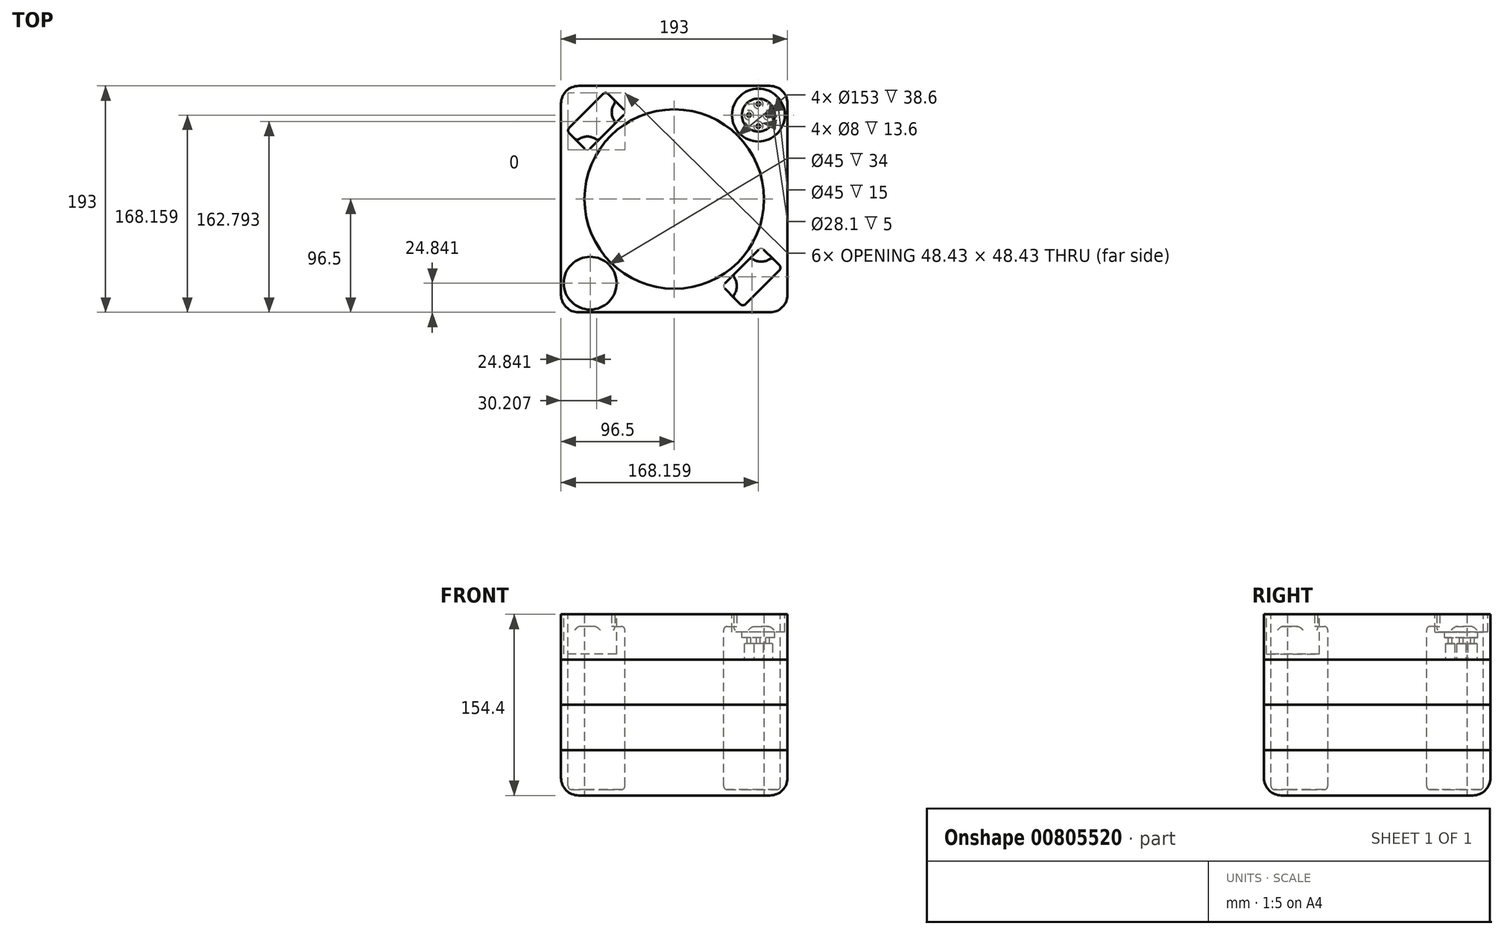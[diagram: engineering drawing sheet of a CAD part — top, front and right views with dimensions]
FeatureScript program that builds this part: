
annotation { "Feature Type Name" : "Feature", "Feature Type Description" : "" }
export const myFeature = defineFeature(function(context is Context, id is Id, definition is map)
    precondition{}
    {
        {
            var Q0;
            Q0=qCreatedBy(makeId("Top.planeOp"),FACE);
            cPlane(context, id + "F0", {"entities" : qUnion([Q0]), "cplaneType" : CPlaneType.OFFSET, "offset" : 0 * mm, "width" : 150 * mm, "height" : 150 * mm});
        }
        {
            var Q0;
            Q0=qCreatedBy(makeId("Top.planeOp"),FACE);
            cPlane(context, id + "F1", {"entities" : qUnion([Q0]), "cplaneType" : CPlaneType.OFFSET, "offset" : 38.6 * mm, "width" : 150 * mm, "height" : 150 * mm});
        }
        {
            var Q0;
            Q0=qCreatedBy(makeId("Top.planeOp"),FACE);
            cPlane(context, id + "F2", {"entities" : qUnion([Q0]), "cplaneType" : CPlaneType.OFFSET, "offset" : 77.2 * mm, "width" : 150 * mm, "height" : 150 * mm});
        }
        {
            var Q0;
            Q0=qCreatedBy(makeId("Top.planeOp"),FACE);
            cPlane(context, id + "F3", {"entities" : qUnion([Q0]), "cplaneType" : CPlaneType.OFFSET, "offset" : 115.8 * mm, "width" : 150 * mm, "height" : 150 * mm});
        }
        {
            var Q0;
            Q0=qCreatedBy(makeId("Top.planeOp"),FACE);
            cPlane(context, id + "F4", {"entities" : qUnion([Q0]), "cplaneType" : CPlaneType.OFFSET, "offset" : 154.4 * mm, "width" : 150 * mm, "height" : 150 * mm});
        }
        {
            var Q0;
            Q0=qCreatedBy(id+"F0.planeOp",FACE);
            cPlane(context, id + "F5", {"entities" : qUnion([Q0]), "cplaneType" : CPlaneType.OFFSET, "offset" : 5 * mm, "width" : 150 * mm, "height" : 150 * mm});
        }
        {
            var Q0;
            Q0=qCreatedBy(id+"F0.planeOp",FACE);
            var sketch = newSketch(context, id + "F6", { "sketchPlane" : qUnion([Q0])});
            skCircle(sketch, "E0", {"center": v(0, 0) * mm, "radius": 76.5 * mm});
            skLineSegment(sketch, "E1.bottom", {"start": v(96.5, 96.5) * mm, "end": v(-96.5, 96.5) * mm});
            skLineSegment(sketch, "E1.top", {"start": v(96.5, -96.5) * mm, "end": v(-96.5, -96.5) * mm});
            skLineSegment(sketch, "E1.left", {"start": v(96.5, 96.5) * mm, "end": v(96.5, -96.5) * mm});
            skLineSegment(sketch, "E1.right", {"start": v(-96.5, 96.5) * mm, "end": v(-96.5, -96.5) * mm});
            skLineSegment(sketch, "E2", {"start": v(-76.5, 0) * mm, "end": v(-96.5, 0) * mm, "construction": true});
            skPoint(sketch, "E2.startSnap0", {"position": v(-96.5, 0) * mm});
            skSolve(sketch);
        }
        {
            var Q0;
            Q0=qCreatedBy(id+"F1.planeOp",FACE);
            var sketch = newSketch(context, id + "F7", { "sketchPlane" : qUnion([Q0])});
            skCircle(sketch, "E3", {"center": v(0, 0) * mm, "radius": 76.5 * mm});
            skLineSegment(sketch, "E4.bottom", {"start": v(96.5, 96.5) * mm, "end": v(-96.5, 96.5) * mm});
            skLineSegment(sketch, "E4.top", {"start": v(96.5, -96.5) * mm, "end": v(-96.5, -96.5) * mm});
            skLineSegment(sketch, "E4.left", {"start": v(96.5, 96.5) * mm, "end": v(96.5, -96.5) * mm});
            skLineSegment(sketch, "E4.right", {"start": v(-96.5, 96.5) * mm, "end": v(-96.5, -96.5) * mm});
            skLineSegment(sketch, "E5", {"start": v(-76.5, 0) * mm, "end": v(-96.5, 0) * mm, "construction": true});
            skPoint(sketch, "E5.startSnap0", {"position": v(-96.5, 0) * mm});
            skSolve(sketch);
        }
        {
            var Q0;
            Q0=qCreatedBy(id+"F2.planeOp",FACE);
            var sketch = newSketch(context, id + "F8", { "sketchPlane" : qUnion([Q0])});
            skCircle(sketch, "E6", {"center": v(0, 0) * mm, "radius": 76.5 * mm});
            skLineSegment(sketch, "E7.bottom", {"start": v(96.5, 96.5) * mm, "end": v(-96.5, 96.5) * mm});
            skLineSegment(sketch, "E7.top", {"start": v(96.5, -96.5) * mm, "end": v(-96.5, -96.5) * mm});
            skLineSegment(sketch, "E7.left", {"start": v(96.5, 96.5) * mm, "end": v(96.5, -96.5) * mm});
            skLineSegment(sketch, "E7.right", {"start": v(-96.5, 96.5) * mm, "end": v(-96.5, -96.5) * mm});
            skLineSegment(sketch, "E8", {"start": v(-76.5, 0) * mm, "end": v(-96.5, 0) * mm, "construction": true});
            skPoint(sketch, "E8.startSnap0", {"position": v(-96.5, 0) * mm});
            skSolve(sketch);
        }
        {
            var Q0;
            Q0=qCreatedBy(id+"F3.planeOp",FACE);
            var sketch = newSketch(context, id + "F9", { "sketchPlane" : qUnion([Q0])});
            skCircle(sketch, "E9", {"center": v(0, 0) * mm, "radius": 76.5 * mm});
            skLineSegment(sketch, "E10.bottom", {"start": v(96.5, 96.5) * mm, "end": v(-96.5, 96.5) * mm});
            skLineSegment(sketch, "E10.top", {"start": v(96.5, -96.5) * mm, "end": v(-96.5, -96.5) * mm});
            skLineSegment(sketch, "E10.left", {"start": v(96.5, 96.5) * mm, "end": v(96.5, -96.5) * mm});
            skLineSegment(sketch, "E10.right", {"start": v(-96.5, 96.5) * mm, "end": v(-96.5, -96.5) * mm});
            skLineSegment(sketch, "E11", {"start": v(-76.5, 0) * mm, "end": v(-96.5, 0) * mm, "construction": true});
            skPoint(sketch, "E11.startSnap0", {"position": v(-96.5, 0) * mm});
            skSolve(sketch);
        }
        {
            var Q0;
            Q0=qCreatedBy(id+"F4.planeOp",FACE);
            var sketch = newSketch(context, id + "F10", { "sketchPlane" : qUnion([Q0])});
            skCircle(sketch, "E12", {"center": v(0, 0) * mm, "radius": 76.5 * mm});
            skLineSegment(sketch, "E13.bottom", {"start": v(96.5, 96.5) * mm, "end": v(-96.5, 96.5) * mm});
            skLineSegment(sketch, "E13.top", {"start": v(96.5, -96.5) * mm, "end": v(-96.5, -96.5) * mm});
            skLineSegment(sketch, "E13.left", {"start": v(96.5, 96.5) * mm, "end": v(96.5, -96.5) * mm});
            skLineSegment(sketch, "E13.right", {"start": v(-96.5, 96.5) * mm, "end": v(-96.5, -96.5) * mm});
            skLineSegment(sketch, "E14", {"start": v(-76.5, 0) * mm, "end": v(-96.5, 0) * mm, "construction": true});
            skPoint(sketch, "E14.startSnap0", {"position": v(-96.5, 0) * mm});
            skSolve(sketch);
        }
        {
            var Q0;
            Q0=qCreatedBy(id+"F5.planeOp",FACE);
            var sketch = newSketch(context, id + "F11", { "sketchPlane" : qUnion([Q0])});
            skCircle(sketch, "E15", {"center": v(0, 0) * mm, "radius": 76.5 * mm, "construction": true});
            skLineSegment(sketch, "E16.bottom", {"start": v(96.5, 96.5) * mm, "end": v(-96.5, 96.5) * mm, "construction": true});
            skLineSegment(sketch, "E16.top", {"start": v(96.5, -96.5) * mm, "end": v(-96.5, -96.5) * mm, "construction": true});
            skLineSegment(sketch, "E16.left", {"start": v(96.5, 96.5) * mm, "end": v(96.5, -96.5) * mm, "construction": true});
            skLineSegment(sketch, "E16.right", {"start": v(-96.5, 96.5) * mm, "end": v(-96.5, -96.5) * mm, "construction": true});
            skLineSegment(sketch, "E17", {"start": v(-57.45, 57.45) * mm, "end": v(-40.84, 74.07) * mm});
            skLineSegment(sketch, "E18", {"start": v(-57.45, 57.45) * mm, "end": v(-74.07, 40.84) * mm});
            skLineSegment(sketch, "E19", {"start": v(-74.07, 40.84) * mm, "end": v(-91.75, 58.51) * mm});
            skLineSegment(sketch, "E20", {"start": v(-76.5, 0) * mm, "end": v(-96.5, 0) * mm, "construction": true});
            skLineSegment(sketch, "E21", {"start": v(-91.75, 58.51) * mm, "end": v(-75.13, 75.13) * mm});
            skLineSegment(sketch, "E22", {"start": v(-75.13, 75.13) * mm, "end": v(-58.51, 91.75) * mm});
            skLineSegment(sketch, "E23", {"start": v(-58.51, 91.75) * mm, "end": v(-40.84, 74.07) * mm});
            skLineSegment(sketch, "E24", {"start": v(-91.75, 58.51) * mm, "end": v(-96.5, 58.51) * mm, "construction": true});
            skLineSegment(sketch, "E25", {"start": v(-58.51, 91.75) * mm, "end": v(-58.51, 96.5) * mm, "construction": true});
            skLineSegment(sketch, "E26", {"start": v(57.45, -57.45) * mm, "end": v(74.07, -40.84) * mm});
            skLineSegment(sketch, "E27", {"start": v(57.45, -57.45) * mm, "end": v(40.84, -74.07) * mm});
            skLineSegment(sketch, "E28", {"start": v(40.84, -74.07) * mm, "end": v(58.51, -91.75) * mm});
            skLineSegment(sketch, "E29", {"start": v(91.75, -58.51) * mm, "end": v(74.07, -40.84) * mm});
            skLineSegment(sketch, "E30", {"start": v(91.75, -58.51) * mm, "end": v(96.5, -58.51) * mm, "construction": true});
            skLineSegment(sketch, "E31", {"start": v(58.51, -91.75) * mm, "end": v(75.13, -75.13) * mm});
            skLineSegment(sketch, "E32", {"start": v(75.13, -75.13) * mm, "end": v(91.75, -58.51) * mm});
            skLineSegment(sketch, "E33", {"start": v(-57.45, 57.45) * mm, "end": v(-54.1, 54.1) * mm, "construction": true});
            skLineSegment(sketch, "E34", {"start": v(57.45, -57.45) * mm, "end": v(54.1, -54.1) * mm, "construction": true});
            skLineSegment(sketch, "E35", {"start": v(58.51, -91.75) * mm, "end": v(58.51, -96.5) * mm, "construction": true});
            skLineSegment(sketch, "E36", {"start": v(54.1, -54.1) * mm, "end": v(60.81, -54.1) * mm, "construction": true});
            skLineSegment(sketch, "E37", {"start": v(-54.1, 54.1) * mm, "end": v(-60.81, 54.1) * mm, "construction": true});
            skCircle(sketch, "E38", {"center": v(-74.07, 40.84) * mm, "radius": 12.5 * mm});
            skCircle(sketch, "E39", {"center": v(-40.84, 74.07) * mm, "radius": 12.5 * mm});
            skCircle(sketch, "E40", {"center": v(40.84, -74.07) * mm, "radius": 12.5 * mm});
            skCircle(sketch, "E41", {"center": v(74.07, -40.84) * mm, "radius": 12.5 * mm});
            skSolve(sketch);
        }
        {
            var Q0;
            Q0=makeQuery(id+"F6.imprint","IMPRINT",FACE,{"disambiguationData":[TD([[makeQuery(id+"F6.imprint","IMPRINT",EDGE,{"derivedFrom":sQuery(id+"F6.wireOp",EDGE,"E0")}),-1.0]])]});
            extrude(context, id + "F12", {"entities" : qUnion([Q0]), "depth" : 38.6 * mm, "offsetDistance" : 25 * mm});
        }
        {
            var Q0;
            Q0=makeQuery(id+"F7.imprint","IMPRINT",FACE,{"disambiguationData":[TD([[makeQuery(id+"F7.imprint","IMPRINT",EDGE,{"derivedFrom":sQuery(id+"F7.wireOp",EDGE,"E3")}),-1.0]])]});
            extrude(context, id + "F13", {"entities" : qUnion([Q0]), "depth" : 38.6 * mm, "offsetDistance" : 25 * mm});
        }
        {
            var Q0;
            Q0=makeQuery(id+"F8.imprint","IMPRINT",FACE,{"disambiguationData":[TD([[makeQuery(id+"F8.imprint","IMPRINT",EDGE,{"derivedFrom":sQuery(id+"F8.wireOp",EDGE,"E6")}),-1.0]])]});
            extrude(context, id + "F14", {"entities" : qUnion([Q0]), "depth" : 38.6 * mm, "offsetDistance" : 25 * mm});
        }
        {
            var Q0;
            Q0=makeQuery(id+"F9.imprint","IMPRINT",FACE,{"disambiguationData":[TD([[makeQuery(id+"F9.imprint","IMPRINT",EDGE,{"derivedFrom":sQuery(id+"F9.wireOp",EDGE,"E9")}),-1.0]])]});
            extrude(context, id + "F15", {"entities" : qUnion([Q0]), "depth" : 38.6 * mm, "offsetDistance" : 25 * mm});
        }
        {
            var Q0;
            Q0=makeQuery(id+"F10.imprint","IMPRINT",FACE,{"disambiguationData":[TD([[makeQuery(id+"F10.imprint","IMPRINT",EDGE,{"derivedFrom":sQuery(id+"F10.wireOp",EDGE,"E12")}),-1.0]])]});
            extrude(context, id + "F16", {"entities" : qUnion([Q0]), "depth" : 38.6 * mm, "offsetDistance" : 25 * mm});
        }
        {
            var Q0;
            {var subQ0=sQuery(id+"F11.wireOp",EDGE,"E28");var subQ1=sQuery(id+"F11.wireOp",EDGE,"E27");var subQ2=makeQuery(id+"F11.imprint","INTERSECT",VERTEX,{"derivedFrom":[subQ1,subQ0]});Q0=makeQuery(id+"F11.imprint","IMPRINT",FACE,{"disambiguationData":[TD([[makeQuery(id+"F11.imprint","IMPRINT",EDGE,{"disambiguationData":[TD([[subQ2,1.0]])],"derivedFrom":subQ1}),1.0]])]});}
            var Q1;
            {var subQ0=sQuery(id+"F11.wireOp",EDGE,"E29");var subQ1=sQuery(id+"F11.wireOp",EDGE,"E26");var subQ2=makeQuery(id+"F11.imprint","INTERSECT",VERTEX,{"derivedFrom":[subQ1,subQ0]});Q1=makeQuery(id+"F11.imprint","IMPRINT",FACE,{"disambiguationData":[TD([[makeQuery(id+"F11.imprint","IMPRINT",EDGE,{"disambiguationData":[TD([[subQ2,1.0]])],"derivedFrom":subQ1}),-1.0]])]});}
            var Q2;
            {var subQ0=sQuery(id+"F11.wireOp",EDGE,"E19");var subQ1=sQuery(id+"F11.wireOp",EDGE,"E18");var subQ2=makeQuery(id+"F11.imprint","INTERSECT",VERTEX,{"derivedFrom":[subQ1,subQ0]});Q2=makeQuery(id+"F11.imprint","IMPRINT",FACE,{"disambiguationData":[TD([[makeQuery(id+"F11.imprint","IMPRINT",EDGE,{"disambiguationData":[TD([[subQ2,1.0]])],"derivedFrom":subQ1}),-1.0]])]});}
            var Q3;
            {var subQ0=sQuery(id+"F11.wireOp",EDGE,"E23");var subQ1=sQuery(id+"F11.wireOp",EDGE,"E17");var subQ2=makeQuery(id+"F11.imprint","INTERSECT",VERTEX,{"derivedFrom":[subQ1,subQ0]});Q3=makeQuery(id+"F11.imprint","IMPRINT",FACE,{"disambiguationData":[TD([[makeQuery(id+"F11.imprint","IMPRINT",EDGE,{"disambiguationData":[TD([[subQ2,1.0]])],"derivedFrom":subQ1}),1.0]])]});}
            extrude(context, id + "F17", {"entities" : qUnion([Q0, Q1, Q2, Q3]), "operationType" : NewBodyOperationType.REMOVE, "depth" : 139 * mm, "offsetDistance" : 25 * mm});
        }
        {
            var Q0;
            {var subQ0=sQuery(id+"F11.wireOp",EDGE,"E21");Q0=makeQuery(id+"F11.imprint","IMPRINT",FACE,{"disambiguationData":[TD([[makeQuery(id+"F11.imprint","IMPRINT",EDGE,{"derivedFrom":subQ0}),-1.0]])]});}
            var Q1;
            {var subQ9=sQuery(id+"F11.wireOp",EDGE,"E31");Q1=makeQuery(id+"F11.imprint","IMPRINT",FACE,{"disambiguationData":[TD([[makeQuery(id+"F11.imprint","IMPRINT",EDGE,{"derivedFrom":subQ9}),1.0]])]});}
            extrude(context, id + "F18", {"entities" : qUnion([Q0, Q1]), "operationType" : NewBodyOperationType.REMOVE, "depth" : 183 * mm, "offsetDistance" : 25 * mm});
        }
        {
            var Q0;
            Q0=qCreatedBy(id+"F4.planeOp",FACE);
            cPlane(context, id + "F19", {"entities" : qUnion([Q0]), "cplaneType" : CPlaneType.OFFSET, "offset" : 29.9 * mm, "width" : 150 * mm, "height" : 150 * mm});
        }
        {
            var Q0;
            Q0=qCreatedBy(id+"F19.planeOp",FACE);
            var sketch = newSketch(context, id + "F20", { "sketchPlane" : qUnion([Q0])});
            skCircle(sketch, "E42", {"center": v(0, 0) * mm, "radius": 76.5 * mm, "construction": true});
            skLineSegment(sketch, "E43.bottom", {"start": v(96.5, 96.5) * mm, "end": v(-96.5, 96.5) * mm, "construction": true});
            skLineSegment(sketch, "E43.top", {"start": v(96.5, -96.5) * mm, "end": v(-96.5, -96.5) * mm, "construction": true});
            skLineSegment(sketch, "E43.left", {"start": v(96.5, 96.5) * mm, "end": v(96.5, -96.5) * mm, "construction": true});
            skLineSegment(sketch, "E43.right", {"start": v(-96.5, 96.5) * mm, "end": v(-96.5, -96.5) * mm, "construction": true});
            skLineSegment(sketch, "E44", {"start": v(-76.5, 0) * mm, "end": v(-96.5, 0) * mm});
            skLineSegment(sketch, "E45", {"start": v(-96.5, 96.5) * mm, "end": v(-54.1, 54.1) * mm});
            skLineSegment(sketch, "E46", {"start": v(54.1, 54.1) * mm, "end": v(96.5, 96.5) * mm});
            skLineSegment(sketch, "E47", {"start": v(76.5, 0) * mm, "end": v(96.5, 0) * mm});
            skLineSegment(sketch, "E48", {"start": v(54.1, -54.1) * mm, "end": v(96.5, -96.5) * mm});
            skLineSegment(sketch, "E49", {"start": v(0, -76.5) * mm, "end": v(0, -96.5) * mm});
            skLineSegment(sketch, "E50", {"start": v(-54.1, -54.1) * mm, "end": v(-96.5, -96.5) * mm});
            skPoint(sketch, "E51", {"position": v(75.3, 75.3) * mm});
            skPoint(sketch, "E52", {"position": v(-75.3, 75.3) * mm});
            skPoint(sketch, "E53", {"position": v(-75.3, -75.3) * mm});
            skPoint(sketch, "E54", {"position": v(75.3, -75.3) * mm});
            skPoint(sketch, "E55", {"position": v(0, -86.5) * mm});
            skPoint(sketch, "E56", {"position": v(86.5, 0) * mm});
            skPoint(sketch, "E57", {"position": v(-86.5, 0) * mm});
            skLineSegment(sketch, "E58", {"start": v(0, 76.5) * mm, "end": v(0, 96.5) * mm});
            skPoint(sketch, "E59", {"position": v(0, 86.5) * mm});
            skFitSpline(sketch, "E60", {"points": [v(-75.3, 75.3) * mm, v(0, 86.5) * mm, v(75.3, 75.3) * mm, v(86.5, 0) * mm, v(75.3, -75.3) * mm, v(0, -86.5) * mm, v(-75.3, -75.3) * mm, v(-86.5, 0) * mm, v(-75.3, 75.3) * mm]});
            skSolve(sketch);
        }
        {
            var Q0;
            Q0=sQuery(id+"F20.wireOp",EDGE,"E47");
            cPoint(context, id + "F21", {"entities" : qUnion([Q0]), "parameter" : 0.5});
        }
        {
            var Q0;
            Q0 = qCreatedBy(id + "F21" ,VERTEX);
            var Q1;
            Q1=sQuery(id+"F20.wireOp",EDGE,"E60");
            cPlane(context, id + "F22", {"entities" : qUnion([Q0, Q1]), "cplaneType" : CPlaneType.CURVE_POINT, "offset" : 25 * mm, "width" : 150 * mm, "height" : 150 * mm});
        }
        {
            var Q0;
            Q0=qCreatedBy(id+"F22.planeOp",FACE);
            var sketch = newSketch(context, id + "F23", { "sketchPlane" : qUnion([Q0])});
            skCircle(sketch, "E61.cCircle", {"center": v(86.74, 185.08) * mm, "radius": 5 * mm, "construction": true});
            skLineSegment(sketch, "E61.0", {"start": v(91.74, 187.97) * mm, "end": v(91.74, 182.2) * mm});
            skLineSegment(sketch, "E61.1", {"start": v(91.74, 182.2) * mm, "end": v(86.74, 179.3) * mm});
            skLineSegment(sketch, "E61.2", {"start": v(86.74, 179.3) * mm, "end": v(81.74, 182.2) * mm});
            skLineSegment(sketch, "E61.3", {"start": v(81.74, 182.2) * mm, "end": v(81.74, 187.97) * mm});
            skLineSegment(sketch, "E61.4", {"start": v(81.74, 187.97) * mm, "end": v(86.74, 190.86) * mm});
            skLineSegment(sketch, "E61.5", {"start": v(86.74, 190.86) * mm, "end": v(91.74, 187.97) * mm});
            skPoint(sketch, "E61.0.midPoint", {"position": v(91.74, 185.08) * mm});
            skSolve(sketch);
        }
        {
            var Q0;
            Q0=makeQuery(id+"F23.imprint","IMPRINT",FACE,{"disambiguationData":[TD([[makeQuery(id+"F23.imprint","IMPRINT",EDGE,{"derivedFrom":sQuery(id+"F23.wireOp",EDGE,"E61.0")}),-1.0]])]});
            var Q1;
            Q1=sQuery(id+"F20.wireOp",EDGE,"E60");
            sweep(context, id + "F24", {"operationType" : NewBodyOperationType.REMOVE, "profiles" : qUnion([Q0]), "path" : qUnion([Q1])});
        }
        {
            var Q0;
            Q0=qCreatedBy(id+"F4.planeOp",FACE);
            var sketch = newSketch(context, id + "F25", { "sketchPlane" : qUnion([Q0])});
            skCircle(sketch, "E62", {"center": v(0, 0) * mm, "radius": 76.5 * mm, "construction": true});
            skLineSegment(sketch, "E63.bottom", {"start": v(96.5, 96.5) * mm, "end": v(-96.5, 96.5) * mm, "construction": true});
            skLineSegment(sketch, "E63.top", {"start": v(96.5, -96.5) * mm, "end": v(-96.5, -96.5) * mm, "construction": true});
            skLineSegment(sketch, "E63.left", {"start": v(96.5, 96.5) * mm, "end": v(96.5, -96.5) * mm, "construction": true});
            skLineSegment(sketch, "E63.right", {"start": v(-96.5, 96.5) * mm, "end": v(-96.5, -96.5) * mm, "construction": true});
            skLineSegment(sketch, "E64", {"start": v(-76.5, 0) * mm, "end": v(-96.5, 0) * mm, "construction": true});
            skCircle(sketch, "E65", {"center": v(-71.66, -71.66) * mm, "radius": 22.5 * mm});
            skLineSegment(sketch, "E66", {"start": v(-71.66, -71.66) * mm, "end": v(-96.5, -71.66) * mm, "construction": true});
            skLineSegment(sketch, "E67", {"start": v(-71.66, -71.66) * mm, "end": v(-71.66, -96.5) * mm, "construction": true});
            skLineSegment(sketch, "E68", {"start": v(-71.66, -71.66) * mm, "end": v(-54.1, -54.1) * mm, "construction": true});
            skCircle(sketch, "E69", {"center": v(-71.66, -71.66) * mm, "radius": 14.05 * mm});
            skLineSegment(sketch, "E70", {"start": v(-71.66, -71.66) * mm, "end": v(-71.66, -62.16) * mm, "construction": true});
            skLineSegment(sketch, "E71", {"start": v(-71.66, -71.66) * mm, "end": v(-71.66, -81.16) * mm, "construction": true});
            skLineSegment(sketch, "E72", {"start": v(-71.66, -71.66) * mm, "end": v(-63.66, -71.66) * mm, "construction": true});
            skLineSegment(sketch, "E73", {"start": v(-71.66, -71.66) * mm, "end": v(-79.66, -71.66) * mm, "construction": true});
            skCircle(sketch, "E74", {"center": v(-71.66, -62.16) * mm, "radius": 1.55 * mm});
            skCircle(sketch, "E75", {"center": v(-79.66, -71.66) * mm, "radius": 1.55 * mm});
            skCircle(sketch, "E76", {"center": v(-71.66, -81.16) * mm, "radius": 1.55 * mm});
            skCircle(sketch, "E77", {"center": v(-63.66, -71.66) * mm, "radius": 1.55 * mm});
            skLineSegment(sketch, "E78", {"start": v(0, 0) * mm, "end": v(-54.1, -54.1) * mm, "construction": true});
            skSolve(sketch);
        }
        {
            var Q0;
            Q0=qCreatedBy(id+"F4.planeOp",FACE);
            var sketch = newSketch(context, id + "F26", { "sketchPlane" : qUnion([Q0])});
            skCircle(sketch, "E79", {"center": v(0, 0) * mm, "radius": 76.5 * mm, "construction": true});
            skLineSegment(sketch, "E80.bottom", {"start": v(-96.5, 96.5) * mm, "end": v(96.5, 96.5) * mm, "construction": true});
            skLineSegment(sketch, "E80.top", {"start": v(-96.5, -96.5) * mm, "end": v(96.5, -96.5) * mm, "construction": true});
            skLineSegment(sketch, "E80.left", {"start": v(-96.5, 96.5) * mm, "end": v(-96.5, -96.5) * mm, "construction": true});
            skLineSegment(sketch, "E80.right", {"start": v(96.5, 96.5) * mm, "end": v(96.5, -96.5) * mm, "construction": true});
            skLineSegment(sketch, "E81", {"start": v(-76.5, 0) * mm, "end": v(-96.5, 0) * mm, "construction": true});
            skCircle(sketch, "E82", {"center": v(71.66, 71.66) * mm, "radius": 22.5 * mm});
            skCircle(sketch, "E83", {"center": v(71.66, 71.66) * mm, "radius": 14.05 * mm});
            skLineSegment(sketch, "E84", {"start": v(71.66, 71.66) * mm, "end": v(54.1, 54.1) * mm, "construction": true});
            skLineSegment(sketch, "E85", {"start": v(71.66, 71.66) * mm, "end": v(71.66, 96.5) * mm, "construction": true});
            skLineSegment(sketch, "E86", {"start": v(71.66, 71.66) * mm, "end": v(96.5, 71.66) * mm, "construction": true});
            skLineSegment(sketch, "E87", {"start": v(0, 0) * mm, "end": v(54.1, 54.1) * mm, "construction": true});
            skLineSegment(sketch, "E88", {"start": v(71.66, 71.66) * mm, "end": v(71.66, 62.16) * mm, "construction": true});
            skPoint(sketch, "E89", {"position": v(79.66, 71.66) * mm});
            skPoint(sketch, "E90", {"position": v(71.66, 81.16) * mm});
            skLineSegment(sketch, "E91", {"start": v(71.66, 71.66) * mm, "end": v(63.66, 71.66) * mm, "construction": true});
            skCircle(sketch, "E92", {"center": v(71.66, 81.16) * mm, "radius": 1.55 * mm});
            skCircle(sketch, "E93", {"center": v(79.66, 71.66) * mm, "radius": 1.55 * mm});
            skCircle(sketch, "E94", {"center": v(63.66, 71.66) * mm, "radius": 1.55 * mm});
            skCircle(sketch, "E95", {"center": v(71.66, 62.16) * mm, "radius": 1.55 * mm});
            skSolve(sketch);
        }
        {
            var Q0;
            Q0=makeQuery(id+"F16.opExtrude","CAP_FACE",FACE,{"disambiguationData":[OSD([sQuery(id+"F10.wireOp",EDGE,"E12"),sQuery(id+"F10.wireOp",EDGE,"E13.bottom"),sQuery(id+"F10.wireOp",EDGE,"E13.top"),sQuery(id+"F10.wireOp",EDGE,"E13.left"),sQuery(id+"F10.wireOp",EDGE,"E13.right")])],"isStart":false});
            var sketch = newSketch(context, id + "F27", { "sketchPlane" : qUnion([Q0])});
            skCircle(sketch, "E96", {"center": v(0, 0) * mm, "radius": 76.5 * mm, "construction": true});
            skLineSegment(sketch, "E97.bottom", {"start": v(96.5, 96.5) * mm, "end": v(-96.5, 96.5) * mm, "construction": true});
            skLineSegment(sketch, "E97.top", {"start": v(96.5, -96.5) * mm, "end": v(-96.5, -96.5) * mm, "construction": true});
            skLineSegment(sketch, "E97.left", {"start": v(96.5, 96.5) * mm, "end": v(96.5, -96.5) * mm, "construction": true});
            skLineSegment(sketch, "E97.right", {"start": v(-96.5, 96.5) * mm, "end": v(-96.5, -96.5) * mm, "construction": true});
            skLineSegment(sketch, "E98", {"start": v(-76.5, 0) * mm, "end": v(-96.5, 0) * mm, "construction": true});
            skCircle(sketch, "E99", {"center": v(-71.66, -71.66) * mm, "radius": 22.5 * mm});
            skLineSegment(sketch, "E100", {"start": v(-71.66, -71.66) * mm, "end": v(-96.5, -71.66) * mm, "construction": true});
            skLineSegment(sketch, "E101", {"start": v(-71.66, -71.66) * mm, "end": v(-71.66, -96.5) * mm, "construction": true});
            skLineSegment(sketch, "E102", {"start": v(-71.66, -71.66) * mm, "end": v(-54.1, -54.1) * mm, "construction": true});
            skCircle(sketch, "E103", {"center": v(-71.66, -71.66) * mm, "radius": 14.05 * mm});
            skLineSegment(sketch, "E104", {"start": v(-71.66, -71.66) * mm, "end": v(-71.66, -62.16) * mm, "construction": true});
            skLineSegment(sketch, "E105", {"start": v(-71.66, -71.66) * mm, "end": v(-71.66, -81.16) * mm, "construction": true});
            skLineSegment(sketch, "E106", {"start": v(-71.66, -71.66) * mm, "end": v(-63.66, -71.66) * mm, "construction": true});
            skLineSegment(sketch, "E107", {"start": v(-71.66, -71.66) * mm, "end": v(-79.66, -71.66) * mm, "construction": true});
            skCircle(sketch, "E108", {"center": v(-71.66, -62.16) * mm, "radius": 4 * mm});
            skCircle(sketch, "E109", {"center": v(-79.66, -71.66) * mm, "radius": 4 * mm});
            skCircle(sketch, "E110", {"center": v(-71.66, -81.16) * mm, "radius": 4 * mm});
            skCircle(sketch, "E111", {"center": v(-63.66, -71.66) * mm, "radius": 4 * mm});
            skLineSegment(sketch, "E112", {"start": v(0, 0) * mm, "end": v(-54.1, -54.1) * mm, "construction": true});
            skSolve(sketch);
        }
        {
            var Q0;
            Q0=qCreatedBy(id+"F3.planeOp",FACE);
            var sketch = newSketch(context, id + "F28", { "sketchPlane" : qUnion([Q0])});
            skCircle(sketch, "E113", {"center": v(0, 0) * mm, "radius": 76.5 * mm, "construction": true});
            skLineSegment(sketch, "E114.bottom", {"start": v(-96.5, 96.5) * mm, "end": v(96.5, 96.5) * mm, "construction": true});
            skLineSegment(sketch, "E114.top", {"start": v(-96.5, -96.5) * mm, "end": v(96.5, -96.5) * mm, "construction": true});
            skLineSegment(sketch, "E114.left", {"start": v(-96.5, 96.5) * mm, "end": v(-96.5, -96.5) * mm, "construction": true});
            skLineSegment(sketch, "E114.right", {"start": v(96.5, 96.5) * mm, "end": v(96.5, -96.5) * mm, "construction": true});
            skLineSegment(sketch, "E115", {"start": v(-76.5, 0) * mm, "end": v(-96.5, 0) * mm, "construction": true});
            skCircle(sketch, "E116", {"center": v(71.66, 71.66) * mm, "radius": 22.5 * mm});
            skCircle(sketch, "E117", {"center": v(71.66, 71.66) * mm, "radius": 14.05 * mm});
            skLineSegment(sketch, "E118", {"start": v(71.66, 71.66) * mm, "end": v(54.1, 54.1) * mm, "construction": true});
            skLineSegment(sketch, "E119", {"start": v(71.66, 71.66) * mm, "end": v(71.66, 96.5) * mm, "construction": true});
            skLineSegment(sketch, "E120", {"start": v(71.66, 71.66) * mm, "end": v(96.5, 71.66) * mm, "construction": true});
            skLineSegment(sketch, "E121", {"start": v(0, 0) * mm, "end": v(54.1, 54.1) * mm, "construction": true});
            skLineSegment(sketch, "E122", {"start": v(71.66, 71.66) * mm, "end": v(71.66, 62.16) * mm, "construction": true});
            skPoint(sketch, "E123", {"position": v(79.66, 71.66) * mm});
            skPoint(sketch, "E124", {"position": v(71.66, 81.16) * mm});
            skLineSegment(sketch, "E125", {"start": v(71.66, 71.66) * mm, "end": v(63.66, 71.66) * mm, "construction": true});
            skCircle(sketch, "E126", {"center": v(71.66, 81.16) * mm, "radius": 4 * mm});
            skCircle(sketch, "E127", {"center": v(79.66, 71.66) * mm, "radius": 4 * mm});
            skCircle(sketch, "E128", {"center": v(63.66, 71.66) * mm, "radius": 4 * mm});
            skCircle(sketch, "E129", {"center": v(71.66, 62.16) * mm, "radius": 4 * mm});
            skSolve(sketch);
        }
        {
            var Q0;
            Q0=makeQuery(id+"F25.imprint","IMPRINT",FACE,{"disambiguationData":[TD([[makeQuery(id+"F25.imprint","IMPRINT",EDGE,{"derivedFrom":sQuery(id+"F25.wireOp",EDGE,"E65")}),1.0]])]});
            var Q1;
            Q1=makeQuery(id+"F25.imprint","IMPRINT",FACE,{"disambiguationData":[TD([[makeQuery(id+"F25.imprint","IMPRINT",EDGE,{"derivedFrom":sQuery(id+"F25.wireOp",EDGE,"E77")}),1.0]])]});
            var Q2;
            Q2=makeQuery(id+"F25.imprint","IMPRINT",FACE,{"disambiguationData":[TD([[makeQuery(id+"F25.imprint","IMPRINT",EDGE,{"derivedFrom":sQuery(id+"F25.wireOp",EDGE,"E74")}),1.0]])]});
            var Q3;
            Q3=makeQuery(id+"F25.imprint","IMPRINT",FACE,{"disambiguationData":[TD([[makeQuery(id+"F25.imprint","IMPRINT",EDGE,{"derivedFrom":sQuery(id+"F25.wireOp",EDGE,"E76")}),1.0]])]});
            var Q4;
            Q4=makeQuery(id+"F25.imprint","IMPRINT",FACE,{"disambiguationData":[TD([[makeQuery(id+"F25.imprint","IMPRINT",EDGE,{"derivedFrom":sQuery(id+"F25.wireOp",EDGE,"E69")}),1.0]])]});
            var Q5;
            Q5=makeQuery(id+"F25.imprint","IMPRINT",FACE,{"disambiguationData":[TD([[makeQuery(id+"F25.imprint","IMPRINT",EDGE,{"derivedFrom":sQuery(id+"F25.wireOp",EDGE,"E75")}),1.0]])]});
            extrude(context, id + "F29", {"entities" : qUnion([Q0, Q1, Q2, Q3, Q4, Q5]), "operationType" : NewBodyOperationType.REMOVE, "oppositeDirection" : true, "depth" : 34 * mm, "offsetDistance" : 25 * mm});
        }
        {
            var Q0;
            Q0=makeQuery(id+"F25.imprint","IMPRINT",FACE,{"disambiguationData":[TD([[makeQuery(id+"F25.imprint","IMPRINT",EDGE,{"derivedFrom":sQuery(id+"F25.wireOp",EDGE,"E75")}),1.0]])]});
            var Q1;
            Q1=makeQuery(id+"F25.imprint","IMPRINT",FACE,{"disambiguationData":[TD([[makeQuery(id+"F25.imprint","IMPRINT",EDGE,{"derivedFrom":sQuery(id+"F25.wireOp",EDGE,"E74")}),1.0]])]});
            var Q2;
            Q2=makeQuery(id+"F25.imprint","IMPRINT",FACE,{"disambiguationData":[TD([[makeQuery(id+"F25.imprint","IMPRINT",EDGE,{"derivedFrom":sQuery(id+"F25.wireOp",EDGE,"E77")}),1.0]])]});
            var Q3;
            Q3=makeQuery(id+"F25.imprint","IMPRINT",FACE,{"disambiguationData":[TD([[makeQuery(id+"F25.imprint","IMPRINT",EDGE,{"derivedFrom":sQuery(id+"F25.wireOp",EDGE,"E76")}),1.0]])]});
            var Q4;
            Q4=makeQuery(id+"F25.imprint","IMPRINT",FACE,{"disambiguationData":[TD([[makeQuery(id+"F25.imprint","IMPRINT",EDGE,{"derivedFrom":sQuery(id+"F25.wireOp",EDGE,"E69")}),1.0]])]});
            extrude(context, id + "F30", {"entities" : qUnion([Q0, Q1, Q2, Q3, Q4]), "operationType" : NewBodyOperationType.REMOVE, "depth" : 5 * mm, "offsetDistance" : 25 * mm});
        }
        {
            var Q0;
            Q0=makeQuery(id+"F25.imprint","IMPRINT",FACE,{"disambiguationData":[TD([[makeQuery(id+"F25.imprint","IMPRINT",EDGE,{"derivedFrom":sQuery(id+"F25.wireOp",EDGE,"E76")}),1.0]])]});
            var Q1;
            Q1=makeQuery(id+"F25.imprint","IMPRINT",FACE,{"disambiguationData":[TD([[makeQuery(id+"F25.imprint","IMPRINT",EDGE,{"derivedFrom":sQuery(id+"F25.wireOp",EDGE,"E77")}),1.0]])]});
            var Q2;
            Q2=makeQuery(id+"F25.imprint","IMPRINT",FACE,{"disambiguationData":[TD([[makeQuery(id+"F25.imprint","IMPRINT",EDGE,{"derivedFrom":sQuery(id+"F25.wireOp",EDGE,"E75")}),1.0]])]});
            var Q3;
            Q3=makeQuery(id+"F25.imprint","IMPRINT",FACE,{"disambiguationData":[TD([[makeQuery(id+"F25.imprint","IMPRINT",EDGE,{"derivedFrom":sQuery(id+"F25.wireOp",EDGE,"E74")}),1.0]])]});
            extrude(context, id + "F31", {"entities" : qUnion([Q0, Q1, Q2, Q3]), "operationType" : NewBodyOperationType.REMOVE, "depth" : 10 * mm, "offsetDistance" : 25 * mm});
        }
        {
            var Q0;
            Q0=makeQuery(id+"F27.imprint","IMPRINT",FACE,{"disambiguationData":[TD([[makeQuery(id+"F27.imprint","IMPRINT",EDGE,{"derivedFrom":sQuery(id+"F27.wireOp",EDGE,"E109")}),1.0]])]});
            var Q1;
            Q1=makeQuery(id+"F27.imprint","IMPRINT",FACE,{"disambiguationData":[TD([[makeQuery(id+"F27.imprint","IMPRINT",EDGE,{"derivedFrom":sQuery(id+"F27.wireOp",EDGE,"E108")}),1.0]])]});
            var Q2;
            Q2=makeQuery(id+"F27.imprint","IMPRINT",FACE,{"disambiguationData":[TD([[makeQuery(id+"F27.imprint","IMPRINT",EDGE,{"derivedFrom":sQuery(id+"F27.wireOp",EDGE,"E111")}),1.0]])]});
            var Q3;
            Q3=makeQuery(id+"F27.imprint","IMPRINT",FACE,{"disambiguationData":[TD([[makeQuery(id+"F27.imprint","IMPRINT",EDGE,{"derivedFrom":sQuery(id+"F27.wireOp",EDGE,"E110")}),1.0]])]});
            extrude(context, id + "F32", {"entities" : qUnion([Q0, Q1, Q2, Q3]), "operationType" : NewBodyOperationType.REMOVE, "oppositeDirection" : true, "depth" : 28.6 * mm, "offsetDistance" : 25 * mm});
        }
        {
            var Q0;
            Q0=makeQuery(id+"F26.imprint","IMPRINT",FACE,{"disambiguationData":[TD([[makeQuery(id+"F26.imprint","IMPRINT",EDGE,{"derivedFrom":sQuery(id+"F26.wireOp",EDGE,"E93")}),1.0]])]});
            var Q1;
            Q1=makeQuery(id+"F26.imprint","IMPRINT",FACE,{"disambiguationData":[TD([[makeQuery(id+"F26.imprint","IMPRINT",EDGE,{"derivedFrom":sQuery(id+"F26.wireOp",EDGE,"E92")}),1.0]])]});
            var Q2;
            Q2=makeQuery(id+"F26.imprint","IMPRINT",FACE,{"disambiguationData":[TD([[makeQuery(id+"F26.imprint","IMPRINT",EDGE,{"derivedFrom":sQuery(id+"F26.wireOp",EDGE,"E95")}),1.0]])]});
            var Q3;
            Q3=makeQuery(id+"F26.imprint","IMPRINT",FACE,{"disambiguationData":[TD([[makeQuery(id+"F26.imprint","IMPRINT",EDGE,{"derivedFrom":sQuery(id+"F26.wireOp",EDGE,"E94")}),1.0]])]});
            var Q4;
            Q4=makeQuery(id+"F26.imprint","IMPRINT",FACE,{"disambiguationData":[TD([[makeQuery(id+"F26.imprint","IMPRINT",EDGE,{"derivedFrom":sQuery(id+"F26.wireOp",EDGE,"E83")}),1.0]])]});
            extrude(context, id + "F33", {"entities" : qUnion([Q0, Q1, Q2, Q3, Q4]), "operationType" : NewBodyOperationType.REMOVE, "oppositeDirection" : true, "depth" : 20 * mm, "offsetDistance" : 25 * mm});
        }
        {
            var Q0;
            Q0=makeQuery(id+"F26.imprint","IMPRINT",FACE,{"disambiguationData":[TD([[makeQuery(id+"F26.imprint","IMPRINT",EDGE,{"derivedFrom":sQuery(id+"F26.wireOp",EDGE,"E95")}),1.0]])]});
            var Q1;
            Q1=makeQuery(id+"F26.imprint","IMPRINT",FACE,{"disambiguationData":[TD([[makeQuery(id+"F26.imprint","IMPRINT",EDGE,{"derivedFrom":sQuery(id+"F26.wireOp",EDGE,"E94")}),1.0]])]});
            var Q2;
            Q2=makeQuery(id+"F26.imprint","IMPRINT",FACE,{"disambiguationData":[TD([[makeQuery(id+"F26.imprint","IMPRINT",EDGE,{"derivedFrom":sQuery(id+"F26.wireOp",EDGE,"E92")}),1.0]])]});
            var Q3;
            Q3=makeQuery(id+"F26.imprint","IMPRINT",FACE,{"disambiguationData":[TD([[makeQuery(id+"F26.imprint","IMPRINT",EDGE,{"derivedFrom":sQuery(id+"F26.wireOp",EDGE,"E93")}),1.0]])]});
            var Q4;
            Q4=makeQuery(id+"F26.imprint","IMPRINT",FACE,{"disambiguationData":[TD([[makeQuery(id+"F26.imprint","IMPRINT",EDGE,{"derivedFrom":sQuery(id+"F26.wireOp",EDGE,"E83")}),1.0]])]});
            var Q5;
            Q5=makeQuery(id+"F26.imprint","IMPRINT",FACE,{"disambiguationData":[TD([[makeQuery(id+"F26.imprint","IMPRINT",EDGE,{"derivedFrom":sQuery(id+"F26.wireOp",EDGE,"E82")}),1.0]])]});
            extrude(context, id + "F34", {"entities" : qUnion([Q0, Q1, Q2, Q3, Q4, Q5]), "operationType" : NewBodyOperationType.REMOVE, "depth" : 19 * mm, "offsetDistance" : 25 * mm});
        }
        {
            var Q0;
            Q0=makeQuery(id+"F26.imprint","IMPRINT",FACE,{"disambiguationData":[TD([[makeQuery(id+"F26.imprint","IMPRINT",EDGE,{"derivedFrom":sQuery(id+"F26.wireOp",EDGE,"E93")}),1.0]])]});
            var Q1;
            Q1=makeQuery(id+"F26.imprint","IMPRINT",FACE,{"disambiguationData":[TD([[makeQuery(id+"F26.imprint","IMPRINT",EDGE,{"derivedFrom":sQuery(id+"F26.wireOp",EDGE,"E92")}),1.0]])]});
            var Q2;
            Q2=makeQuery(id+"F26.imprint","IMPRINT",FACE,{"disambiguationData":[TD([[makeQuery(id+"F26.imprint","IMPRINT",EDGE,{"derivedFrom":sQuery(id+"F26.wireOp",EDGE,"E94")}),1.0]])]});
            var Q3;
            Q3=makeQuery(id+"F26.imprint","IMPRINT",FACE,{"disambiguationData":[TD([[makeQuery(id+"F26.imprint","IMPRINT",EDGE,{"derivedFrom":sQuery(id+"F26.wireOp",EDGE,"E95")}),1.0]])]});
            var Q4;
            Q4=makeQuery(id+"F26.imprint","IMPRINT",FACE,{"disambiguationData":[TD([[makeQuery(id+"F26.imprint","IMPRINT",EDGE,{"derivedFrom":sQuery(id+"F26.wireOp",EDGE,"E83")}),1.0]])]});
            var Q5;
            Q5=makeQuery(id+"F26.imprint","IMPRINT",FACE,{"disambiguationData":[TD([[makeQuery(id+"F26.imprint","IMPRINT",EDGE,{"derivedFrom":sQuery(id+"F26.wireOp",EDGE,"E82")}),1.0]])]});
            extrude(context, id + "F35", {"entities" : qUnion([Q0, Q1, Q2, Q3, Q4, Q5]), "operationType" : NewBodyOperationType.REMOVE, "oppositeDirection" : true, "depth" : 15 * mm, "offsetDistance" : 25 * mm});
        }
        {
            var Q0;
            Q0=makeQuery(id+"F26.imprint","IMPRINT",FACE,{"disambiguationData":[TD([[makeQuery(id+"F26.imprint","IMPRINT",EDGE,{"derivedFrom":sQuery(id+"F26.wireOp",EDGE,"E94")}),1.0]])]});
            var Q1;
            Q1=makeQuery(id+"F26.imprint","IMPRINT",FACE,{"disambiguationData":[TD([[makeQuery(id+"F26.imprint","IMPRINT",EDGE,{"derivedFrom":sQuery(id+"F26.wireOp",EDGE,"E92")}),1.0]])]});
            var Q2;
            Q2=makeQuery(id+"F26.imprint","IMPRINT",FACE,{"disambiguationData":[TD([[makeQuery(id+"F26.imprint","IMPRINT",EDGE,{"derivedFrom":sQuery(id+"F26.wireOp",EDGE,"E93")}),1.0]])]});
            var Q3;
            Q3=makeQuery(id+"F26.imprint","IMPRINT",FACE,{"disambiguationData":[TD([[makeQuery(id+"F26.imprint","IMPRINT",EDGE,{"derivedFrom":sQuery(id+"F26.wireOp",EDGE,"E95")}),1.0]])]});
            extrude(context, id + "F36", {"entities" : qUnion([Q0, Q1, Q2, Q3]), "operationType" : NewBodyOperationType.REMOVE, "oppositeDirection" : true, "depth" : 25 * mm, "offsetDistance" : 25 * mm});
        }
        {
            var Q0;
            Q0=makeQuery(id+"F28.imprint","IMPRINT",FACE,{"disambiguationData":[TD([[makeQuery(id+"F28.imprint","IMPRINT",EDGE,{"derivedFrom":sQuery(id+"F28.wireOp",EDGE,"E126")}),1.0]])]});
            var Q1;
            Q1=makeQuery(id+"F28.imprint","IMPRINT",FACE,{"disambiguationData":[TD([[makeQuery(id+"F28.imprint","IMPRINT",EDGE,{"derivedFrom":sQuery(id+"F28.wireOp",EDGE,"E128")}),1.0]])]});
            var Q2;
            Q2=makeQuery(id+"F28.imprint","IMPRINT",FACE,{"disambiguationData":[TD([[makeQuery(id+"F28.imprint","IMPRINT",EDGE,{"derivedFrom":sQuery(id+"F28.wireOp",EDGE,"E129")}),1.0]])]});
            var Q3;
            Q3=makeQuery(id+"F28.imprint","IMPRINT",FACE,{"disambiguationData":[TD([[makeQuery(id+"F28.imprint","IMPRINT",EDGE,{"derivedFrom":sQuery(id+"F28.wireOp",EDGE,"E127")}),1.0]])]});
            extrude(context, id + "F37", {"entities" : qUnion([Q0, Q1, Q2, Q3]), "operationType" : NewBodyOperationType.REMOVE, "depth" : 13.6 * mm, "offsetDistance" : 25 * mm});
        }
        {
            var Q0;
            Q0=makeQuery(id+"F16.opExtrude","SWEPT_EDGE",EDGE,{"disambiguationData":[OSD([sQuery(id+"F10.wireOp",EDGE,"E13.top"),sQuery(id+"F10.wireOp",EDGE,"E13.right")])]});
            var Q1;
            Q1=makeQuery(id+"F15.opExtrude","SWEPT_EDGE",EDGE,{"disambiguationData":[OSD([sQuery(id+"F9.wireOp",EDGE,"E10.top"),sQuery(id+"F9.wireOp",EDGE,"E10.right")])]});
            var Q2;
            Q2=makeQuery(id+"F16.opExtrude","SWEPT_EDGE",EDGE,{"disambiguationData":[OSD([sQuery(id+"F10.wireOp",EDGE,"E13.top"),sQuery(id+"F10.wireOp",EDGE,"E13.left")])]});
            var Q3;
            Q3=makeQuery(id+"F15.opExtrude","SWEPT_EDGE",EDGE,{"disambiguationData":[OSD([sQuery(id+"F9.wireOp",EDGE,"E10.top"),sQuery(id+"F9.wireOp",EDGE,"E10.left")])]});
            var Q4;
            Q4=makeQuery(id+"F16.opExtrude","SWEPT_EDGE",EDGE,{"disambiguationData":[OSD([sQuery(id+"F10.wireOp",EDGE,"E13.bottom"),sQuery(id+"F10.wireOp",EDGE,"E13.left")])]});
            var Q5;
            Q5=makeQuery(id+"F15.opExtrude","SWEPT_EDGE",EDGE,{"disambiguationData":[OSD([sQuery(id+"F9.wireOp",EDGE,"E10.bottom"),sQuery(id+"F9.wireOp",EDGE,"E10.left")])]});
            var Q6;
            Q6=makeQuery(id+"F15.opExtrude","SWEPT_EDGE",EDGE,{"disambiguationData":[OSD([sQuery(id+"F9.wireOp",EDGE,"E10.bottom"),sQuery(id+"F9.wireOp",EDGE,"E10.right")])]});
            var Q7;
            Q7=makeQuery(id+"F16.opExtrude","SWEPT_EDGE",EDGE,{"disambiguationData":[OSD([sQuery(id+"F10.wireOp",EDGE,"E13.bottom"),sQuery(id+"F10.wireOp",EDGE,"E13.right")])]});
            var Q8;
            Q8=makeQuery(id+"F16.opExtrude","CAP_EDGE",EDGE,{"disambiguationData":[OSD([sQuery(id+"F10.wireOp",EDGE,"E13.right")])],"isStart":false});
            var Q9;
            Q9=makeQuery(id+"F16.opExtrude","CAP_EDGE",EDGE,{"disambiguationData":[OSD([sQuery(id+"F10.wireOp",EDGE,"E13.bottom")])],"isStart":false});
            var Q10;
            Q10=makeQuery(id+"F16.opExtrude","CAP_EDGE",EDGE,{"disambiguationData":[OSD([sQuery(id+"F10.wireOp",EDGE,"E13.left")])],"isStart":false});
            var Q11;
            Q11=makeQuery(id+"F16.opExtrude","CAP_EDGE",EDGE,{"disambiguationData":[OSD([sQuery(id+"F10.wireOp",EDGE,"E13.top")])],"isStart":false});
            var Q12;
            Q12=makeQuery(id+"F14.opExtrude","SWEPT_EDGE",EDGE,{"disambiguationData":[OSD([sQuery(id+"F8.wireOp",EDGE,"E7.top"),sQuery(id+"F8.wireOp",EDGE,"E7.left")])]});
            var Q13;
            Q13=makeQuery(id+"F13.opExtrude","SWEPT_EDGE",EDGE,{"disambiguationData":[OSD([sQuery(id+"F7.wireOp",EDGE,"E4.top"),sQuery(id+"F7.wireOp",EDGE,"E4.left")])]});
            var Q14;
            Q14=makeQuery(id+"F12.opExtrude","SWEPT_EDGE",EDGE,{"disambiguationData":[OSD([sQuery(id+"F6.wireOp",EDGE,"E1.top"),sQuery(id+"F6.wireOp",EDGE,"E1.left")])]});
            var Q15;
            Q15=makeQuery(id+"F12.opExtrude","SWEPT_EDGE",EDGE,{"disambiguationData":[OSD([sQuery(id+"F6.wireOp",EDGE,"E1.top"),sQuery(id+"F6.wireOp",EDGE,"E1.right")])]});
            var Q16;
            Q16=makeQuery(id+"F13.opExtrude","SWEPT_EDGE",EDGE,{"disambiguationData":[OSD([sQuery(id+"F7.wireOp",EDGE,"E4.top"),sQuery(id+"F7.wireOp",EDGE,"E4.right")])]});
            var Q17;
            Q17=makeQuery(id+"F14.opExtrude","SWEPT_EDGE",EDGE,{"disambiguationData":[OSD([sQuery(id+"F8.wireOp",EDGE,"E7.top"),sQuery(id+"F8.wireOp",EDGE,"E7.right")])]});
            var Q18;
            Q18=makeQuery(id+"F14.opExtrude","SWEPT_EDGE",EDGE,{"disambiguationData":[OSD([sQuery(id+"F8.wireOp",EDGE,"E7.bottom"),sQuery(id+"F8.wireOp",EDGE,"E7.left")])]});
            var Q19;
            Q19=makeQuery(id+"F13.opExtrude","SWEPT_EDGE",EDGE,{"disambiguationData":[OSD([sQuery(id+"F7.wireOp",EDGE,"E4.bottom"),sQuery(id+"F7.wireOp",EDGE,"E4.left")])]});
            var Q20;
            Q20=makeQuery(id+"F12.opExtrude","SWEPT_EDGE",EDGE,{"disambiguationData":[OSD([sQuery(id+"F6.wireOp",EDGE,"E1.bottom"),sQuery(id+"F6.wireOp",EDGE,"E1.left")])]});
            var Q21;
            Q21=makeQuery(id+"F14.opExtrude","SWEPT_EDGE",EDGE,{"disambiguationData":[OSD([sQuery(id+"F8.wireOp",EDGE,"E7.bottom"),sQuery(id+"F8.wireOp",EDGE,"E7.right")])]});
            var Q22;
            Q22=makeQuery(id+"F13.opExtrude","SWEPT_EDGE",EDGE,{"disambiguationData":[OSD([sQuery(id+"F7.wireOp",EDGE,"E4.bottom"),sQuery(id+"F7.wireOp",EDGE,"E4.right")])]});
            var Q23;
            Q23=makeQuery(id+"F12.opExtrude","SWEPT_EDGE",EDGE,{"disambiguationData":[OSD([sQuery(id+"F6.wireOp",EDGE,"E1.bottom"),sQuery(id+"F6.wireOp",EDGE,"E1.right")])]});
            var Q24;
            Q24=makeQuery(id+"F12.opExtrude","CAP_EDGE",EDGE,{"disambiguationData":[OSD([sQuery(id+"F6.wireOp",EDGE,"E1.left")])],"isStart":true});
            var Q25;
            Q25=makeQuery(id+"F12.opExtrude","CAP_EDGE",EDGE,{"disambiguationData":[OSD([sQuery(id+"F6.wireOp",EDGE,"E1.bottom")])],"isStart":true});
            var Q26;
            Q26=makeQuery(id+"F12.opExtrude","CAP_EDGE",EDGE,{"disambiguationData":[OSD([sQuery(id+"F6.wireOp",EDGE,"E1.right")])],"isStart":true});
            var Q27;
            Q27=makeQuery(id+"F12.opExtrude","CAP_EDGE",EDGE,{"disambiguationData":[OSD([sQuery(id+"F6.wireOp",EDGE,"E1.top")])],"isStart":true});
            fillet(context, id + "F38", {"entities" : qUnion([Q0, Q1, Q2, Q3, Q4, Q5, Q6, Q7, Q8, Q9, Q10, Q11, Q12, Q13, Q14, Q15, Q16, Q17, Q18, Q19, Q20, Q21, Q22, Q23, Q24, Q25, Q26, Q27]), "radius" : 15 * mm, "tangentPropagation" : true, "allowEdgeOverflow" : false});
        }
        {
            var Q0;
            Q0=makeQuery(id+"F16.opExtrude","CAP_EDGE",EDGE,{"disambiguationData":[OSD([sQuery(id+"F10.wireOp",EDGE,"E12")])],"isStart":false});
            chamfer(context, id + "F39", {"entities" : qUnion([Q0]), "width" : 5 * mm, "tangentPropagation" : true});
        }
        {
            var Q0;
            {var subQ0=sQuery(id+"F11.wireOp",EDGE,"E26");var subQ1=sQuery(id+"F11.wireOp",EDGE,"E29");Q0=makeQuery(id+"F17.boolean.opBoolean","COPY",EDGE,{"disambiguationData":[TD([makeQuery(id+"F17.opExtrude","CAP_FACE",FACE,{"disambiguationData":[OSD([subQ0,subQ1,sQuery(id+"F11.wireOp",EDGE,"E41")])],"isStart":false})])],"derivedFrom":makeQuery(id+"F17.opExtrude","SWEPT_EDGE",EDGE,{"disambiguationData":[OSD([subQ0,subQ1])]})});}
            var Q1;
            Q1=makeQuery(id+"F17.boolean.opBoolean","COPY",EDGE,{"derivedFrom":makeQuery(id+"F17.opExtrude","CAP_EDGE",EDGE,{"disambiguationData":[OSD([sQuery(id+"F11.wireOp",EDGE,"E26")])],"isStart":false})});
            var Q2;
            Q2=makeQuery(id+"F17.boolean.opBoolean","COPY",EDGE,{"derivedFrom":makeQuery(id+"F17.opExtrude","CAP_EDGE",EDGE,{"disambiguationData":[OSD([sQuery(id+"F11.wireOp",EDGE,"E29")])],"isStart":false})});
            var Q3;
            {var subQ0=sQuery(id+"F11.wireOp",EDGE,"E41");var subQ1=sQuery(id+"F11.wireOp",EDGE,"E26");var subQ2=sQuery(id+"F11.wireOp",EDGE,"E29");var subQ3=sQuery(id+"F11.wireOp",EDGE,"E32");Q3=makeQuery(id+"F18.boolean.opBoolean","COPY",EDGE,{"disambiguationData":[topologyDisambiguationEdgeConnected([makeQuery(id+"F17.boolean.opBoolean","COPY",FACE,{"disambiguationData":[TD([makeQuery(id+"F17.opExtrude","CAP_FACE",FACE,{"disambiguationData":[OSD([subQ1,subQ2,subQ0])],"isStart":false})])],"derivedFrom":makeQuery(id+"F17.opExtrude","SWEPT_FACE",FACE,{"disambiguationData":[OSD([subQ2])]})}),makeQuery(id+"F18.opExtrude","SWEPT_FACE",FACE,{"disambiguationData":[OSD([subQ2])]}),makeQuery(id+"F18.opExtrude","SWEPT_FACE",FACE,{"disambiguationData":[OSD([sQuery(id+"F11.wireOp",EDGE,"E31"),subQ3])]})])],"derivedFrom":makeQuery(id+"F18.opExtrude","SWEPT_EDGE",EDGE,{"disambiguationData":[OSD([subQ2,subQ3])]})});}
            var Q4;
            {var subQ0=sQuery(id+"F11.wireOp",EDGE,"E29");var subQ1=sQuery(id+"F11.wireOp",EDGE,"E32");Q4=makeQuery(id+"F18.boolean.opBoolean","COPY",EDGE,{"disambiguationData":[topologyDisambiguationEdgeConnected([makeQuery(id+"F18.opExtrude","SWEPT_FACE",FACE,{"disambiguationData":[OSD([subQ0])]}),makeQuery(id+"F18.opExtrude","SWEPT_FACE",FACE,{"disambiguationData":[OSD([sQuery(id+"F11.wireOp",EDGE,"E31"),subQ1])]})])],"derivedFrom":makeQuery(id+"F18.opExtrude","SWEPT_EDGE",EDGE,{"disambiguationData":[OSD([subQ0,subQ1])]})});}
            var Q5;
            {var subQ0=sQuery(id+"F11.wireOp",EDGE,"E41");var subQ1=sQuery(id+"F11.wireOp",EDGE,"E26");var subQ2=sQuery(id+"F11.wireOp",EDGE,"E29");Q5=makeQuery(id+"F18.boolean.opBoolean","COPY",EDGE,{"disambiguationData":[topologyDisambiguationEdgeConnected([makeQuery(id+"F17.boolean.opBoolean","COPY",FACE,{"disambiguationData":[TD([makeQuery(id+"F17.opExtrude","CAP_FACE",FACE,{"disambiguationData":[OSD([subQ1,subQ2,subQ0])],"isStart":false})])],"derivedFrom":makeQuery(id+"F17.opExtrude","SWEPT_FACE",FACE,{"disambiguationData":[OSD([subQ2])]})}),makeQuery(id+"F18.opExtrude","SWEPT_FACE",FACE,{"disambiguationData":[OSD([subQ2])]}),makeQuery(id+"F18.opExtrude","SWEPT_FACE",FACE,{"disambiguationData":[OSD([subQ0])]})])],"derivedFrom":makeQuery(id+"F18.opExtrude","SWEPT_EDGE",EDGE,{"disambiguationData":[OSD([subQ2,subQ0])]})});}
            var Q6;
            {var subQ0=sQuery(id+"F11.wireOp",EDGE,"E29");var subQ1=sQuery(id+"F11.wireOp",EDGE,"E41");Q6=makeQuery(id+"F18.boolean.opBoolean","COPY",EDGE,{"disambiguationData":[topologyDisambiguationEdgeConnected([makeQuery(id+"F18.opExtrude","SWEPT_FACE",FACE,{"disambiguationData":[OSD([subQ0])]}),makeQuery(id+"F18.opExtrude","SWEPT_FACE",FACE,{"disambiguationData":[OSD([subQ1])]})])],"derivedFrom":makeQuery(id+"F18.opExtrude","SWEPT_EDGE",EDGE,{"disambiguationData":[OSD([subQ0,subQ1])]})});}
            var Q7;
            {var subQ1=sQuery(id+"F11.wireOp",EDGE,"E41");var subQ2=sQuery(id+"F11.wireOp",EDGE,"E29");var subQ3=sQuery(id+"F11.wireOp",EDGE,"E26");var subQ4=sQuery(id+"F11.wireOp",EDGE,"E28");var subQ5=sQuery(id+"F11.wireOp",EDGE,"E40");var subQ6=sQuery(id+"F11.wireOp",EDGE,"E27");Q7=makeQuery(id+"F18.boolean.opBoolean","COPY",EDGE,{"disambiguationData":[topologyDisambiguationEdgeConnected([makeQuery(id+"F17.boolean.opBoolean","COPY",FACE,{"disambiguationData":[TD([makeQuery(id+"F17.opExtrude","CAP_FACE",FACE,{"disambiguationData":[OSD([subQ3,subQ2,subQ1])],"isStart":false})])],"derivedFrom":makeQuery(id+"F17.opExtrude","SWEPT_FACE",FACE,{"disambiguationData":[OSD([subQ3])]})}),makeQuery(id+"F17.boolean.opBoolean","COPY",FACE,{"disambiguationData":[TD([makeQuery(id+"F17.opExtrude","CAP_FACE",FACE,{"disambiguationData":[OSD([subQ6,subQ4,subQ5])],"isStart":false})])],"derivedFrom":makeQuery(id+"F17.opExtrude","SWEPT_FACE",FACE,{"disambiguationData":[OSD([subQ6])]})}),makeQuery(id+"F18.opExtrude","SWEPT_FACE",FACE,{"disambiguationData":[OSD([subQ3,subQ6])]}),makeQuery(id+"F18.opExtrude","SWEPT_FACE",FACE,{"disambiguationData":[OSD([subQ1])]})])],"derivedFrom":makeQuery(id+"F18.opExtrude","SWEPT_EDGE",EDGE,{"disambiguationData":[OSD([subQ3,subQ1])]})});}
            var Q8;
            {var subQ0=sQuery(id+"F11.wireOp",EDGE,"E26");var subQ1=sQuery(id+"F11.wireOp",EDGE,"E41");Q8=makeQuery(id+"F18.boolean.opBoolean","COPY",EDGE,{"disambiguationData":[topologyDisambiguationEdgeConnected([makeQuery(id+"F18.opExtrude","SWEPT_FACE",FACE,{"disambiguationData":[OSD([subQ0,sQuery(id+"F11.wireOp",EDGE,"E27")])]}),makeQuery(id+"F18.opExtrude","SWEPT_FACE",FACE,{"disambiguationData":[OSD([subQ1])]})])],"derivedFrom":makeQuery(id+"F18.opExtrude","SWEPT_EDGE",EDGE,{"disambiguationData":[OSD([subQ0,subQ1])]})});}
            var Q9;
            {var subQ0=sQuery(id+"F11.wireOp",EDGE,"E28");var subQ1=sQuery(id+"F11.wireOp",EDGE,"E27");Q9=makeQuery(id+"F17.boolean.opBoolean","COPY",EDGE,{"disambiguationData":[TD([makeQuery(id+"F17.opExtrude","CAP_FACE",FACE,{"disambiguationData":[OSD([subQ1,subQ0,sQuery(id+"F11.wireOp",EDGE,"E40")])],"isStart":false})])],"derivedFrom":makeQuery(id+"F17.opExtrude","SWEPT_EDGE",EDGE,{"disambiguationData":[OSD([subQ1,subQ0])]})});}
            var Q10;
            Q10=makeQuery(id+"F17.boolean.opBoolean","COPY",EDGE,{"derivedFrom":makeQuery(id+"F17.opExtrude","CAP_EDGE",EDGE,{"disambiguationData":[OSD([sQuery(id+"F11.wireOp",EDGE,"E27")])],"isStart":false})});
            var Q11;
            Q11=makeQuery(id+"F17.boolean.opBoolean","COPY",EDGE,{"derivedFrom":makeQuery(id+"F17.opExtrude","CAP_EDGE",EDGE,{"disambiguationData":[OSD([sQuery(id+"F11.wireOp",EDGE,"E28")])],"isStart":false})});
            var Q12;
            {var subQ0=sQuery(id+"F11.wireOp",EDGE,"E27");var subQ1=sQuery(id+"F11.wireOp",EDGE,"E40");Q12=makeQuery(id+"F18.boolean.opBoolean","COPY",EDGE,{"disambiguationData":[topologyDisambiguationEdgeConnected([makeQuery(id+"F18.opExtrude","SWEPT_FACE",FACE,{"disambiguationData":[OSD([sQuery(id+"F11.wireOp",EDGE,"E26"),subQ0])]}),makeQuery(id+"F18.opExtrude","SWEPT_FACE",FACE,{"disambiguationData":[OSD([subQ1])]})])],"derivedFrom":makeQuery(id+"F18.opExtrude","SWEPT_EDGE",EDGE,{"disambiguationData":[OSD([subQ0,subQ1])]})});}
            var Q13;
            {var subQ1=sQuery(id+"F11.wireOp",EDGE,"E41");var subQ2=sQuery(id+"F11.wireOp",EDGE,"E29");var subQ3=sQuery(id+"F11.wireOp",EDGE,"E26");var subQ4=sQuery(id+"F11.wireOp",EDGE,"E28");var subQ5=sQuery(id+"F11.wireOp",EDGE,"E40");var subQ6=sQuery(id+"F11.wireOp",EDGE,"E27");Q13=makeQuery(id+"F18.boolean.opBoolean","COPY",EDGE,{"disambiguationData":[topologyDisambiguationEdgeConnected([makeQuery(id+"F17.boolean.opBoolean","COPY",FACE,{"disambiguationData":[TD([makeQuery(id+"F17.opExtrude","CAP_FACE",FACE,{"disambiguationData":[OSD([subQ3,subQ2,subQ1])],"isStart":false})])],"derivedFrom":makeQuery(id+"F17.opExtrude","SWEPT_FACE",FACE,{"disambiguationData":[OSD([subQ3])]})}),makeQuery(id+"F17.boolean.opBoolean","COPY",FACE,{"disambiguationData":[TD([makeQuery(id+"F17.opExtrude","CAP_FACE",FACE,{"disambiguationData":[OSD([subQ6,subQ4,subQ5])],"isStart":false})])],"derivedFrom":makeQuery(id+"F17.opExtrude","SWEPT_FACE",FACE,{"disambiguationData":[OSD([subQ6])]})}),makeQuery(id+"F18.opExtrude","SWEPT_FACE",FACE,{"disambiguationData":[OSD([subQ3,subQ6])]}),makeQuery(id+"F18.opExtrude","SWEPT_FACE",FACE,{"disambiguationData":[OSD([subQ5])]})])],"derivedFrom":makeQuery(id+"F18.opExtrude","SWEPT_EDGE",EDGE,{"disambiguationData":[OSD([subQ6,subQ5])]})});}
            var Q14;
            {var subQ0=sQuery(id+"F11.wireOp",EDGE,"E27");var subQ1=sQuery(id+"F11.wireOp",EDGE,"E40");var subQ2=sQuery(id+"F11.wireOp",EDGE,"E28");Q14=makeQuery(id+"F18.boolean.opBoolean","COPY",EDGE,{"disambiguationData":[topologyDisambiguationEdgeConnected([makeQuery(id+"F17.boolean.opBoolean","COPY",FACE,{"disambiguationData":[TD([makeQuery(id+"F17.opExtrude","CAP_FACE",FACE,{"disambiguationData":[OSD([subQ0,subQ2,subQ1])],"isStart":false})])],"derivedFrom":makeQuery(id+"F17.opExtrude","SWEPT_FACE",FACE,{"disambiguationData":[OSD([subQ2])]})}),makeQuery(id+"F18.opExtrude","SWEPT_FACE",FACE,{"disambiguationData":[OSD([subQ2])]}),makeQuery(id+"F18.opExtrude","SWEPT_FACE",FACE,{"disambiguationData":[OSD([subQ1])]})])],"derivedFrom":makeQuery(id+"F18.opExtrude","SWEPT_EDGE",EDGE,{"disambiguationData":[OSD([subQ2,subQ1])]})});}
            var Q15;
            {var subQ0=sQuery(id+"F11.wireOp",EDGE,"E28");var subQ1=sQuery(id+"F11.wireOp",EDGE,"E40");Q15=makeQuery(id+"F18.boolean.opBoolean","COPY",EDGE,{"disambiguationData":[topologyDisambiguationEdgeConnected([makeQuery(id+"F18.opExtrude","SWEPT_FACE",FACE,{"disambiguationData":[OSD([subQ0])]}),makeQuery(id+"F18.opExtrude","SWEPT_FACE",FACE,{"disambiguationData":[OSD([subQ1])]})])],"derivedFrom":makeQuery(id+"F18.opExtrude","SWEPT_EDGE",EDGE,{"disambiguationData":[OSD([subQ0,subQ1])]})});}
            var Q16;
            {var subQ0=sQuery(id+"F11.wireOp",EDGE,"E28");var subQ1=sQuery(id+"F11.wireOp",EDGE,"E31");Q16=makeQuery(id+"F18.boolean.opBoolean","COPY",EDGE,{"disambiguationData":[topologyDisambiguationEdgeConnected([makeQuery(id+"F18.opExtrude","SWEPT_FACE",FACE,{"disambiguationData":[OSD([subQ0])]}),makeQuery(id+"F18.opExtrude","SWEPT_FACE",FACE,{"disambiguationData":[OSD([subQ1,sQuery(id+"F11.wireOp",EDGE,"E32")])]})])],"derivedFrom":makeQuery(id+"F18.opExtrude","SWEPT_EDGE",EDGE,{"disambiguationData":[OSD([subQ0,subQ1])]})});}
            var Q17;
            {var subQ0=sQuery(id+"F11.wireOp",EDGE,"E27");var subQ1=sQuery(id+"F11.wireOp",EDGE,"E40");var subQ2=sQuery(id+"F11.wireOp",EDGE,"E28");var subQ3=sQuery(id+"F11.wireOp",EDGE,"E31");Q17=makeQuery(id+"F18.boolean.opBoolean","COPY",EDGE,{"disambiguationData":[topologyDisambiguationEdgeConnected([makeQuery(id+"F17.boolean.opBoolean","COPY",FACE,{"disambiguationData":[TD([makeQuery(id+"F17.opExtrude","CAP_FACE",FACE,{"disambiguationData":[OSD([subQ0,subQ2,subQ1])],"isStart":false})])],"derivedFrom":makeQuery(id+"F17.opExtrude","SWEPT_FACE",FACE,{"disambiguationData":[OSD([subQ2])]})}),makeQuery(id+"F18.opExtrude","SWEPT_FACE",FACE,{"disambiguationData":[OSD([subQ2])]}),makeQuery(id+"F18.opExtrude","SWEPT_FACE",FACE,{"disambiguationData":[OSD([subQ3,sQuery(id+"F11.wireOp",EDGE,"E32")])]})])],"derivedFrom":makeQuery(id+"F18.opExtrude","SWEPT_EDGE",EDGE,{"disambiguationData":[OSD([subQ2,subQ3])]})});}
            var Q18;
            {var subQ0=sQuery(id+"F8.wireOp",EDGE,"E7.right");var subQ1=sQuery(id+"F8.wireOp",EDGE,"E7.left");var subQ2=sQuery(id+"F8.wireOp",EDGE,"E7.top");var subQ3=sQuery(id+"F8.wireOp",EDGE,"E7.bottom");var subQ4=sQuery(id+"F8.wireOp",EDGE,"E6");var subQ5=sQuery(id+"F11.wireOp",EDGE,"E28");var subQ6=sQuery(id+"F11.wireOp",EDGE,"E27");Q18=makeQuery(id+"F17.boolean.opBoolean","COPY",EDGE,{"disambiguationData":[TD([makeQuery(id+"F14.opExtrude","CAP_FACE",FACE,{"disambiguationData":[OSD([subQ4,subQ3,subQ2,subQ1,subQ0])],"isStart":true})])],"derivedFrom":makeQuery(id+"F17.opExtrude","SWEPT_EDGE",EDGE,{"disambiguationData":[OSD([subQ6,subQ5])]})});}
            var Q19;
            {var subQ0=sQuery(id+"F8.wireOp",EDGE,"E7.right");var subQ1=sQuery(id+"F8.wireOp",EDGE,"E7.left");var subQ2=sQuery(id+"F8.wireOp",EDGE,"E7.top");var subQ3=sQuery(id+"F8.wireOp",EDGE,"E7.bottom");var subQ4=sQuery(id+"F8.wireOp",EDGE,"E6");var subQ5=sQuery(id+"F11.wireOp",EDGE,"E26");var subQ6=sQuery(id+"F11.wireOp",EDGE,"E29");Q19=makeQuery(id+"F17.boolean.opBoolean","COPY",EDGE,{"disambiguationData":[TD([makeQuery(id+"F14.opExtrude","CAP_FACE",FACE,{"disambiguationData":[OSD([subQ4,subQ3,subQ2,subQ1,subQ0])],"isStart":true})])],"derivedFrom":makeQuery(id+"F17.opExtrude","SWEPT_EDGE",EDGE,{"disambiguationData":[OSD([subQ5,subQ6])]})});}
            var Q20;
            {var subQ0=sQuery(id+"F8.wireOp",EDGE,"E7.right");var subQ1=sQuery(id+"F8.wireOp",EDGE,"E7.left");var subQ2=sQuery(id+"F8.wireOp",EDGE,"E7.top");var subQ3=sQuery(id+"F8.wireOp",EDGE,"E7.bottom");var subQ4=sQuery(id+"F8.wireOp",EDGE,"E6");var subQ5=sQuery(id+"F11.wireOp",EDGE,"E29");var subQ6=sQuery(id+"F11.wireOp",EDGE,"E32");Q20=makeQuery(id+"F18.boolean.opBoolean","COPY",EDGE,{"disambiguationData":[topologyDisambiguationEdgeConnected([makeQuery(id+"F17.boolean.opBoolean","COPY",FACE,{"disambiguationData":[TD([makeQuery(id+"F14.opExtrude","CAP_FACE",FACE,{"disambiguationData":[OSD([subQ4,subQ3,subQ2,subQ1,subQ0])],"isStart":true})])],"derivedFrom":makeQuery(id+"F17.opExtrude","SWEPT_FACE",FACE,{"disambiguationData":[OSD([subQ5])]})}),makeQuery(id+"F18.opExtrude","SWEPT_FACE",FACE,{"disambiguationData":[OSD([subQ5])]}),makeQuery(id+"F18.opExtrude","SWEPT_FACE",FACE,{"disambiguationData":[OSD([sQuery(id+"F11.wireOp",EDGE,"E31"),subQ6])]})])],"derivedFrom":makeQuery(id+"F18.opExtrude","SWEPT_EDGE",EDGE,{"disambiguationData":[OSD([subQ5,subQ6])]})});}
            var Q21;
            {var subQ0=sQuery(id+"F8.wireOp",EDGE,"E7.right");var subQ1=sQuery(id+"F8.wireOp",EDGE,"E7.left");var subQ2=sQuery(id+"F8.wireOp",EDGE,"E7.top");var subQ3=sQuery(id+"F8.wireOp",EDGE,"E7.bottom");var subQ4=sQuery(id+"F8.wireOp",EDGE,"E6");var subQ5=sQuery(id+"F11.wireOp",EDGE,"E28");var subQ6=sQuery(id+"F11.wireOp",EDGE,"E31");Q21=makeQuery(id+"F18.boolean.opBoolean","COPY",EDGE,{"disambiguationData":[topologyDisambiguationEdgeConnected([makeQuery(id+"F17.boolean.opBoolean","COPY",FACE,{"disambiguationData":[TD([makeQuery(id+"F14.opExtrude","CAP_FACE",FACE,{"disambiguationData":[OSD([subQ4,subQ3,subQ2,subQ1,subQ0])],"isStart":true})])],"derivedFrom":makeQuery(id+"F17.opExtrude","SWEPT_FACE",FACE,{"disambiguationData":[OSD([subQ5])]})}),makeQuery(id+"F18.opExtrude","SWEPT_FACE",FACE,{"disambiguationData":[OSD([subQ5])]}),makeQuery(id+"F18.opExtrude","SWEPT_FACE",FACE,{"disambiguationData":[OSD([subQ6,sQuery(id+"F11.wireOp",EDGE,"E32")])]})])],"derivedFrom":makeQuery(id+"F18.opExtrude","SWEPT_EDGE",EDGE,{"disambiguationData":[OSD([subQ5,subQ6])]})});}
            var Q22;
            {var subQ0=sQuery(id+"F7.wireOp",EDGE,"E4.right");var subQ1=sQuery(id+"F7.wireOp",EDGE,"E4.left");var subQ2=sQuery(id+"F7.wireOp",EDGE,"E4.top");var subQ3=sQuery(id+"F7.wireOp",EDGE,"E4.bottom");var subQ4=sQuery(id+"F7.wireOp",EDGE,"E3");var subQ5=sQuery(id+"F11.wireOp",EDGE,"E28");var subQ6=sQuery(id+"F11.wireOp",EDGE,"E31");Q22=makeQuery(id+"F18.boolean.opBoolean","COPY",EDGE,{"disambiguationData":[topologyDisambiguationEdgeConnected([makeQuery(id+"F17.boolean.opBoolean","COPY",FACE,{"disambiguationData":[TD([makeQuery(id+"F13.opExtrude","CAP_FACE",FACE,{"disambiguationData":[OSD([subQ4,subQ3,subQ2,subQ1,subQ0])],"isStart":true})])],"derivedFrom":makeQuery(id+"F17.opExtrude","SWEPT_FACE",FACE,{"disambiguationData":[OSD([subQ5])]})}),makeQuery(id+"F18.opExtrude","SWEPT_FACE",FACE,{"disambiguationData":[OSD([subQ5])]}),makeQuery(id+"F18.opExtrude","SWEPT_FACE",FACE,{"disambiguationData":[OSD([subQ6,sQuery(id+"F11.wireOp",EDGE,"E32")])]})])],"derivedFrom":makeQuery(id+"F18.opExtrude","SWEPT_EDGE",EDGE,{"disambiguationData":[OSD([subQ5,subQ6])]})});}
            var Q23;
            {var subQ0=sQuery(id+"F7.wireOp",EDGE,"E4.right");var subQ1=sQuery(id+"F7.wireOp",EDGE,"E4.left");var subQ2=sQuery(id+"F7.wireOp",EDGE,"E4.top");var subQ3=sQuery(id+"F7.wireOp",EDGE,"E4.bottom");var subQ4=sQuery(id+"F7.wireOp",EDGE,"E3");var subQ5=sQuery(id+"F11.wireOp",EDGE,"E27");var subQ6=sQuery(id+"F11.wireOp",EDGE,"E28");Q23=makeQuery(id+"F17.boolean.opBoolean","COPY",EDGE,{"disambiguationData":[TD([makeQuery(id+"F13.opExtrude","CAP_FACE",FACE,{"disambiguationData":[OSD([subQ4,subQ3,subQ2,subQ1,subQ0])],"isStart":true})])],"derivedFrom":makeQuery(id+"F17.opExtrude","SWEPT_EDGE",EDGE,{"disambiguationData":[OSD([subQ5,subQ6])]})});}
            var Q24;
            {var subQ0=sQuery(id+"F7.wireOp",EDGE,"E4.right");var subQ1=sQuery(id+"F7.wireOp",EDGE,"E4.left");var subQ2=sQuery(id+"F7.wireOp",EDGE,"E4.top");var subQ3=sQuery(id+"F7.wireOp",EDGE,"E4.bottom");var subQ4=sQuery(id+"F7.wireOp",EDGE,"E3");var subQ5=sQuery(id+"F11.wireOp",EDGE,"E29");var subQ6=sQuery(id+"F11.wireOp",EDGE,"E32");Q24=makeQuery(id+"F18.boolean.opBoolean","COPY",EDGE,{"disambiguationData":[topologyDisambiguationEdgeConnected([makeQuery(id+"F17.boolean.opBoolean","COPY",FACE,{"disambiguationData":[TD([makeQuery(id+"F13.opExtrude","CAP_FACE",FACE,{"disambiguationData":[OSD([subQ4,subQ3,subQ2,subQ1,subQ0])],"isStart":true})])],"derivedFrom":makeQuery(id+"F17.opExtrude","SWEPT_FACE",FACE,{"disambiguationData":[OSD([subQ5])]})}),makeQuery(id+"F18.opExtrude","SWEPT_FACE",FACE,{"disambiguationData":[OSD([subQ5])]}),makeQuery(id+"F18.opExtrude","SWEPT_FACE",FACE,{"disambiguationData":[OSD([sQuery(id+"F11.wireOp",EDGE,"E31"),subQ6])]})])],"derivedFrom":makeQuery(id+"F18.opExtrude","SWEPT_EDGE",EDGE,{"disambiguationData":[OSD([subQ5,subQ6])]})});}
            var Q25;
            {var subQ0=sQuery(id+"F7.wireOp",EDGE,"E4.right");var subQ1=sQuery(id+"F7.wireOp",EDGE,"E4.left");var subQ2=sQuery(id+"F7.wireOp",EDGE,"E4.top");var subQ3=sQuery(id+"F7.wireOp",EDGE,"E4.bottom");var subQ4=sQuery(id+"F7.wireOp",EDGE,"E3");var subQ5=sQuery(id+"F11.wireOp",EDGE,"E26");var subQ6=sQuery(id+"F11.wireOp",EDGE,"E29");Q25=makeQuery(id+"F17.boolean.opBoolean","COPY",EDGE,{"disambiguationData":[TD([makeQuery(id+"F13.opExtrude","CAP_FACE",FACE,{"disambiguationData":[OSD([subQ4,subQ3,subQ2,subQ1,subQ0])],"isStart":true})])],"derivedFrom":makeQuery(id+"F17.opExtrude","SWEPT_EDGE",EDGE,{"disambiguationData":[OSD([subQ5,subQ6])]})});}
            var Q26;
            {var subQ0=sQuery(id+"F11.wireOp",EDGE,"E26");var subQ1=sQuery(id+"F11.wireOp",EDGE,"E29");Q26=makeQuery(id+"F17.boolean.opBoolean","COPY",EDGE,{"disambiguationData":[TD([makeQuery(id+"F17.opExtrude","CAP_FACE",FACE,{"disambiguationData":[OSD([subQ0,subQ1,sQuery(id+"F11.wireOp",EDGE,"E41")])],"isStart":true})])],"derivedFrom":makeQuery(id+"F17.opExtrude","SWEPT_EDGE",EDGE,{"disambiguationData":[OSD([subQ0,subQ1])]})});}
            var Q27;
            {var subQ0=sQuery(id+"F11.wireOp",EDGE,"E27");var subQ1=sQuery(id+"F11.wireOp",EDGE,"E26");Q27=makeQuery(id+"F18.boolean.opBoolean","MERGE",EDGE,{"derivedFrom":[makeQuery(id+"F17.boolean.opBoolean","COPY",EDGE,{"derivedFrom":makeQuery(id+"F17.opExtrude","CAP_EDGE",EDGE,{"disambiguationData":[OSD([subQ1])],"isStart":true})}),makeQuery(id+"F17.boolean.opBoolean","COPY",EDGE,{"derivedFrom":makeQuery(id+"F17.opExtrude","CAP_EDGE",EDGE,{"disambiguationData":[OSD([subQ0])],"isStart":true})}),makeQuery(id+"F18.opExtrude","CAP_EDGE",EDGE,{"disambiguationData":[OSD([subQ1,subQ0])],"isStart":true})]});}
            var Q28;
            {var subQ0=sQuery(id+"F11.wireOp",EDGE,"E28");var subQ1=sQuery(id+"F11.wireOp",EDGE,"E27");Q28=makeQuery(id+"F17.boolean.opBoolean","COPY",EDGE,{"disambiguationData":[TD([makeQuery(id+"F17.opExtrude","CAP_FACE",FACE,{"disambiguationData":[OSD([subQ1,subQ0,sQuery(id+"F11.wireOp",EDGE,"E40")])],"isStart":true})])],"derivedFrom":makeQuery(id+"F17.opExtrude","SWEPT_EDGE",EDGE,{"disambiguationData":[OSD([subQ1,subQ0])]})});}
            var Q29;
            {var subQ0=sQuery(id+"F11.wireOp",EDGE,"E28");Q29=makeQuery(id+"F18.boolean.opBoolean","MERGE",EDGE,{"derivedFrom":[makeQuery(id+"F17.boolean.opBoolean","COPY",EDGE,{"derivedFrom":makeQuery(id+"F17.opExtrude","CAP_EDGE",EDGE,{"disambiguationData":[OSD([subQ0])],"isStart":true})}),makeQuery(id+"F18.opExtrude","CAP_EDGE",EDGE,{"disambiguationData":[OSD([subQ0])],"isStart":true})]});}
            var Q30;
            Q30=makeQuery(id+"F18.boolean.opBoolean","COPY",EDGE,{"derivedFrom":makeQuery(id+"F18.opExtrude","CAP_EDGE",EDGE,{"disambiguationData":[OSD([sQuery(id+"F11.wireOp",EDGE,"E31"),sQuery(id+"F11.wireOp",EDGE,"E32")])],"isStart":true})});
            var Q31;
            {var subQ0=sQuery(id+"F11.wireOp",EDGE,"E40");var subQ1=sQuery(id+"F11.wireOp",EDGE,"E28");var subQ2=sQuery(id+"F11.wireOp",EDGE,"E27");var subQ3=sQuery(id+"F11.wireOp",EDGE,"E31");Q31=makeQuery(id+"F18.boolean.opBoolean","COPY",EDGE,{"disambiguationData":[topologyDisambiguationEdgeConnected([makeQuery(id+"F17.boolean.opBoolean","COPY",FACE,{"disambiguationData":[TD([makeQuery(id+"F17.opExtrude","CAP_FACE",FACE,{"disambiguationData":[OSD([subQ2,subQ1,subQ0])],"isStart":true})])],"derivedFrom":makeQuery(id+"F17.opExtrude","SWEPT_FACE",FACE,{"disambiguationData":[OSD([subQ1])]})}),makeQuery(id+"F18.opExtrude","SWEPT_FACE",FACE,{"disambiguationData":[OSD([subQ1])]}),makeQuery(id+"F18.opExtrude","SWEPT_FACE",FACE,{"disambiguationData":[OSD([subQ3,sQuery(id+"F11.wireOp",EDGE,"E32")])]})])],"derivedFrom":makeQuery(id+"F18.opExtrude","SWEPT_EDGE",EDGE,{"disambiguationData":[OSD([subQ1,subQ3])]})});}
            var Q32;
            {var subQ0=sQuery(id+"F11.wireOp",EDGE,"E26");var subQ1=sQuery(id+"F11.wireOp",EDGE,"E41");var subQ2=sQuery(id+"F11.wireOp",EDGE,"E29");var subQ3=sQuery(id+"F11.wireOp",EDGE,"E32");Q32=makeQuery(id+"F18.boolean.opBoolean","COPY",EDGE,{"disambiguationData":[topologyDisambiguationEdgeConnected([makeQuery(id+"F17.boolean.opBoolean","COPY",FACE,{"disambiguationData":[TD([makeQuery(id+"F17.opExtrude","CAP_FACE",FACE,{"disambiguationData":[OSD([subQ0,subQ2,subQ1])],"isStart":true})])],"derivedFrom":makeQuery(id+"F17.opExtrude","SWEPT_FACE",FACE,{"disambiguationData":[OSD([subQ2])]})}),makeQuery(id+"F18.opExtrude","SWEPT_FACE",FACE,{"disambiguationData":[OSD([subQ2])]}),makeQuery(id+"F18.opExtrude","SWEPT_FACE",FACE,{"disambiguationData":[OSD([sQuery(id+"F11.wireOp",EDGE,"E31"),subQ3])]})])],"derivedFrom":makeQuery(id+"F18.opExtrude","SWEPT_EDGE",EDGE,{"disambiguationData":[OSD([subQ2,subQ3])]})});}
            var Q33;
            {var subQ0=sQuery(id+"F11.wireOp",EDGE,"E29");Q33=makeQuery(id+"F18.boolean.opBoolean","MERGE",EDGE,{"derivedFrom":[makeQuery(id+"F17.boolean.opBoolean","COPY",EDGE,{"derivedFrom":makeQuery(id+"F17.opExtrude","CAP_EDGE",EDGE,{"disambiguationData":[OSD([subQ0])],"isStart":true})}),makeQuery(id+"F18.opExtrude","CAP_EDGE",EDGE,{"disambiguationData":[OSD([subQ0])],"isStart":true})]});}
            var Q34;
            {var subQ0=sQuery(id+"F11.wireOp",EDGE,"E23");var subQ1=sQuery(id+"F11.wireOp",EDGE,"E17");Q34=makeQuery(id+"F17.boolean.opBoolean","COPY",EDGE,{"disambiguationData":[TD([makeQuery(id+"F17.opExtrude","CAP_FACE",FACE,{"disambiguationData":[OSD([subQ1,subQ0,sQuery(id+"F11.wireOp",EDGE,"E39")])],"isStart":true})])],"derivedFrom":makeQuery(id+"F17.opExtrude","SWEPT_EDGE",EDGE,{"disambiguationData":[OSD([subQ1,subQ0])]})});}
            var Q35;
            {var subQ0=sQuery(id+"F11.wireOp",EDGE,"E39");var subQ1=sQuery(id+"F11.wireOp",EDGE,"E17");var subQ2=sQuery(id+"F11.wireOp",EDGE,"E23");var subQ3=sQuery(id+"F11.wireOp",EDGE,"E22");Q35=makeQuery(id+"F18.boolean.opBoolean","COPY",EDGE,{"disambiguationData":[topologyDisambiguationEdgeConnected([makeQuery(id+"F17.boolean.opBoolean","COPY",FACE,{"disambiguationData":[TD([makeQuery(id+"F17.opExtrude","CAP_FACE",FACE,{"disambiguationData":[OSD([subQ1,subQ2,subQ0])],"isStart":true})])],"derivedFrom":makeQuery(id+"F17.opExtrude","SWEPT_FACE",FACE,{"disambiguationData":[OSD([subQ2])]})}),makeQuery(id+"F18.opExtrude","SWEPT_FACE",FACE,{"disambiguationData":[OSD([sQuery(id+"F11.wireOp",EDGE,"E21"),subQ3])]}),makeQuery(id+"F18.opExtrude","SWEPT_FACE",FACE,{"disambiguationData":[OSD([subQ2])]})])],"derivedFrom":makeQuery(id+"F18.opExtrude","SWEPT_EDGE",EDGE,{"disambiguationData":[OSD([subQ3,subQ2])]})});}
            var Q36;
            {var subQ0=sQuery(id+"F11.wireOp",EDGE,"E18");var subQ1=sQuery(id+"F11.wireOp",EDGE,"E19");Q36=makeQuery(id+"F17.boolean.opBoolean","COPY",EDGE,{"disambiguationData":[TD([makeQuery(id+"F17.opExtrude","CAP_FACE",FACE,{"disambiguationData":[OSD([subQ0,subQ1,sQuery(id+"F11.wireOp",EDGE,"E38")])],"isStart":true})])],"derivedFrom":makeQuery(id+"F17.opExtrude","SWEPT_EDGE",EDGE,{"disambiguationData":[OSD([subQ0,subQ1])]})});}
            var Q37;
            {var subQ0=sQuery(id+"F11.wireOp",EDGE,"E18");var subQ1=sQuery(id+"F11.wireOp",EDGE,"E38");var subQ2=sQuery(id+"F11.wireOp",EDGE,"E19");var subQ3=sQuery(id+"F11.wireOp",EDGE,"E21");Q37=makeQuery(id+"F18.boolean.opBoolean","COPY",EDGE,{"disambiguationData":[topologyDisambiguationEdgeConnected([makeQuery(id+"F17.boolean.opBoolean","COPY",FACE,{"disambiguationData":[TD([makeQuery(id+"F17.opExtrude","CAP_FACE",FACE,{"disambiguationData":[OSD([subQ0,subQ2,subQ1])],"isStart":true})])],"derivedFrom":makeQuery(id+"F17.opExtrude","SWEPT_FACE",FACE,{"disambiguationData":[OSD([subQ2])]})}),makeQuery(id+"F18.opExtrude","SWEPT_FACE",FACE,{"disambiguationData":[OSD([subQ2])]}),makeQuery(id+"F18.opExtrude","SWEPT_FACE",FACE,{"disambiguationData":[OSD([subQ3,sQuery(id+"F11.wireOp",EDGE,"E22")])]})])],"derivedFrom":makeQuery(id+"F18.opExtrude","SWEPT_EDGE",EDGE,{"disambiguationData":[OSD([subQ2,subQ3])]})});}
            var Q38;
            Q38=makeQuery(id+"F18.boolean.opBoolean","COPY",EDGE,{"derivedFrom":makeQuery(id+"F18.opExtrude","CAP_EDGE",EDGE,{"disambiguationData":[OSD([sQuery(id+"F11.wireOp",EDGE,"E21"),sQuery(id+"F11.wireOp",EDGE,"E22")])],"isStart":true})});
            var Q39;
            {var subQ0=sQuery(id+"F11.wireOp",EDGE,"E19");Q39=makeQuery(id+"F18.boolean.opBoolean","MERGE",EDGE,{"derivedFrom":[makeQuery(id+"F17.boolean.opBoolean","COPY",EDGE,{"derivedFrom":makeQuery(id+"F17.opExtrude","CAP_EDGE",EDGE,{"disambiguationData":[OSD([subQ0])],"isStart":true})}),makeQuery(id+"F18.opExtrude","CAP_EDGE",EDGE,{"disambiguationData":[OSD([subQ0])],"isStart":true})]});}
            var Q40;
            {var subQ0=sQuery(id+"F11.wireOp",EDGE,"E18");var subQ1=sQuery(id+"F11.wireOp",EDGE,"E17");Q40=makeQuery(id+"F18.boolean.opBoolean","MERGE",EDGE,{"derivedFrom":[makeQuery(id+"F17.boolean.opBoolean","COPY",EDGE,{"derivedFrom":makeQuery(id+"F17.opExtrude","CAP_EDGE",EDGE,{"disambiguationData":[OSD([subQ1])],"isStart":true})}),makeQuery(id+"F17.boolean.opBoolean","COPY",EDGE,{"derivedFrom":makeQuery(id+"F17.opExtrude","CAP_EDGE",EDGE,{"disambiguationData":[OSD([subQ0])],"isStart":true})}),makeQuery(id+"F18.opExtrude","CAP_EDGE",EDGE,{"disambiguationData":[OSD([subQ1,subQ0])],"isStart":true})]});}
            var Q41;
            {var subQ0=sQuery(id+"F11.wireOp",EDGE,"E23");Q41=makeQuery(id+"F18.boolean.opBoolean","MERGE",EDGE,{"derivedFrom":[makeQuery(id+"F17.boolean.opBoolean","COPY",EDGE,{"derivedFrom":makeQuery(id+"F17.opExtrude","CAP_EDGE",EDGE,{"disambiguationData":[OSD([subQ0])],"isStart":true})}),makeQuery(id+"F18.opExtrude","CAP_EDGE",EDGE,{"disambiguationData":[OSD([subQ0])],"isStart":true})]});}
            var Q42;
            {var subQ0=sQuery(id+"F7.wireOp",EDGE,"E4.right");var subQ1=sQuery(id+"F7.wireOp",EDGE,"E4.left");var subQ2=sQuery(id+"F7.wireOp",EDGE,"E4.top");var subQ3=sQuery(id+"F7.wireOp",EDGE,"E4.bottom");var subQ4=sQuery(id+"F7.wireOp",EDGE,"E3");var subQ5=sQuery(id+"F11.wireOp",EDGE,"E23");var subQ6=sQuery(id+"F11.wireOp",EDGE,"E17");Q42=makeQuery(id+"F17.boolean.opBoolean","COPY",EDGE,{"disambiguationData":[TD([makeQuery(id+"F13.opExtrude","CAP_FACE",FACE,{"disambiguationData":[OSD([subQ4,subQ3,subQ2,subQ1,subQ0])],"isStart":true})])],"derivedFrom":makeQuery(id+"F17.opExtrude","SWEPT_EDGE",EDGE,{"disambiguationData":[OSD([subQ6,subQ5])]})});}
            var Q43;
            {var subQ0=sQuery(id+"F7.wireOp",EDGE,"E4.right");var subQ1=sQuery(id+"F7.wireOp",EDGE,"E4.left");var subQ2=sQuery(id+"F7.wireOp",EDGE,"E4.top");var subQ3=sQuery(id+"F7.wireOp",EDGE,"E4.bottom");var subQ4=sQuery(id+"F7.wireOp",EDGE,"E3");var subQ5=sQuery(id+"F11.wireOp",EDGE,"E18");var subQ6=sQuery(id+"F11.wireOp",EDGE,"E19");Q43=makeQuery(id+"F17.boolean.opBoolean","COPY",EDGE,{"disambiguationData":[TD([makeQuery(id+"F13.opExtrude","CAP_FACE",FACE,{"disambiguationData":[OSD([subQ4,subQ3,subQ2,subQ1,subQ0])],"isStart":true})])],"derivedFrom":makeQuery(id+"F17.opExtrude","SWEPT_EDGE",EDGE,{"disambiguationData":[OSD([subQ5,subQ6])]})});}
            var Q44;
            {var subQ0=sQuery(id+"F7.wireOp",EDGE,"E4.right");var subQ1=sQuery(id+"F7.wireOp",EDGE,"E4.left");var subQ2=sQuery(id+"F7.wireOp",EDGE,"E4.top");var subQ3=sQuery(id+"F7.wireOp",EDGE,"E4.bottom");var subQ4=sQuery(id+"F7.wireOp",EDGE,"E3");var subQ5=sQuery(id+"F11.wireOp",EDGE,"E23");var subQ6=sQuery(id+"F11.wireOp",EDGE,"E22");Q44=makeQuery(id+"F18.boolean.opBoolean","COPY",EDGE,{"disambiguationData":[topologyDisambiguationEdgeConnected([makeQuery(id+"F17.boolean.opBoolean","COPY",FACE,{"disambiguationData":[TD([makeQuery(id+"F13.opExtrude","CAP_FACE",FACE,{"disambiguationData":[OSD([subQ4,subQ3,subQ2,subQ1,subQ0])],"isStart":true})])],"derivedFrom":makeQuery(id+"F17.opExtrude","SWEPT_FACE",FACE,{"disambiguationData":[OSD([subQ5])]})}),makeQuery(id+"F18.opExtrude","SWEPT_FACE",FACE,{"disambiguationData":[OSD([sQuery(id+"F11.wireOp",EDGE,"E21"),subQ6])]}),makeQuery(id+"F18.opExtrude","SWEPT_FACE",FACE,{"disambiguationData":[OSD([subQ5])]})])],"derivedFrom":makeQuery(id+"F18.opExtrude","SWEPT_EDGE",EDGE,{"disambiguationData":[OSD([subQ6,subQ5])]})});}
            var Q45;
            {var subQ0=sQuery(id+"F7.wireOp",EDGE,"E4.right");var subQ1=sQuery(id+"F7.wireOp",EDGE,"E4.left");var subQ2=sQuery(id+"F7.wireOp",EDGE,"E4.top");var subQ3=sQuery(id+"F7.wireOp",EDGE,"E4.bottom");var subQ4=sQuery(id+"F7.wireOp",EDGE,"E3");var subQ5=sQuery(id+"F11.wireOp",EDGE,"E19");var subQ6=sQuery(id+"F11.wireOp",EDGE,"E21");Q45=makeQuery(id+"F18.boolean.opBoolean","COPY",EDGE,{"disambiguationData":[topologyDisambiguationEdgeConnected([makeQuery(id+"F17.boolean.opBoolean","COPY",FACE,{"disambiguationData":[TD([makeQuery(id+"F13.opExtrude","CAP_FACE",FACE,{"disambiguationData":[OSD([subQ4,subQ3,subQ2,subQ1,subQ0])],"isStart":true})])],"derivedFrom":makeQuery(id+"F17.opExtrude","SWEPT_FACE",FACE,{"disambiguationData":[OSD([subQ5])]})}),makeQuery(id+"F18.opExtrude","SWEPT_FACE",FACE,{"disambiguationData":[OSD([subQ5])]}),makeQuery(id+"F18.opExtrude","SWEPT_FACE",FACE,{"disambiguationData":[OSD([subQ6,sQuery(id+"F11.wireOp",EDGE,"E22")])]})])],"derivedFrom":makeQuery(id+"F18.opExtrude","SWEPT_EDGE",EDGE,{"disambiguationData":[OSD([subQ5,subQ6])]})});}
            var Q46;
            {var subQ0=sQuery(id+"F8.wireOp",EDGE,"E7.right");var subQ1=sQuery(id+"F8.wireOp",EDGE,"E7.left");var subQ2=sQuery(id+"F8.wireOp",EDGE,"E7.top");var subQ3=sQuery(id+"F8.wireOp",EDGE,"E7.bottom");var subQ4=sQuery(id+"F8.wireOp",EDGE,"E6");var subQ5=sQuery(id+"F11.wireOp",EDGE,"E18");var subQ6=sQuery(id+"F11.wireOp",EDGE,"E19");Q46=makeQuery(id+"F17.boolean.opBoolean","COPY",EDGE,{"disambiguationData":[TD([makeQuery(id+"F14.opExtrude","CAP_FACE",FACE,{"disambiguationData":[OSD([subQ4,subQ3,subQ2,subQ1,subQ0])],"isStart":true})])],"derivedFrom":makeQuery(id+"F17.opExtrude","SWEPT_EDGE",EDGE,{"disambiguationData":[OSD([subQ5,subQ6])]})});}
            var Q47;
            {var subQ0=sQuery(id+"F8.wireOp",EDGE,"E7.right");var subQ1=sQuery(id+"F8.wireOp",EDGE,"E7.left");var subQ2=sQuery(id+"F8.wireOp",EDGE,"E7.top");var subQ3=sQuery(id+"F8.wireOp",EDGE,"E7.bottom");var subQ4=sQuery(id+"F8.wireOp",EDGE,"E6");var subQ5=sQuery(id+"F11.wireOp",EDGE,"E19");var subQ6=sQuery(id+"F11.wireOp",EDGE,"E21");Q47=makeQuery(id+"F18.boolean.opBoolean","COPY",EDGE,{"disambiguationData":[topologyDisambiguationEdgeConnected([makeQuery(id+"F17.boolean.opBoolean","COPY",FACE,{"disambiguationData":[TD([makeQuery(id+"F14.opExtrude","CAP_FACE",FACE,{"disambiguationData":[OSD([subQ4,subQ3,subQ2,subQ1,subQ0])],"isStart":true})])],"derivedFrom":makeQuery(id+"F17.opExtrude","SWEPT_FACE",FACE,{"disambiguationData":[OSD([subQ5])]})}),makeQuery(id+"F18.opExtrude","SWEPT_FACE",FACE,{"disambiguationData":[OSD([subQ5])]}),makeQuery(id+"F18.opExtrude","SWEPT_FACE",FACE,{"disambiguationData":[OSD([subQ6,sQuery(id+"F11.wireOp",EDGE,"E22")])]})])],"derivedFrom":makeQuery(id+"F18.opExtrude","SWEPT_EDGE",EDGE,{"disambiguationData":[OSD([subQ5,subQ6])]})});}
            var Q48;
            {var subQ0=sQuery(id+"F8.wireOp",EDGE,"E7.right");var subQ1=sQuery(id+"F8.wireOp",EDGE,"E7.left");var subQ2=sQuery(id+"F8.wireOp",EDGE,"E7.top");var subQ3=sQuery(id+"F8.wireOp",EDGE,"E7.bottom");var subQ4=sQuery(id+"F8.wireOp",EDGE,"E6");var subQ5=sQuery(id+"F11.wireOp",EDGE,"E23");var subQ6=sQuery(id+"F11.wireOp",EDGE,"E22");Q48=makeQuery(id+"F18.boolean.opBoolean","COPY",EDGE,{"disambiguationData":[topologyDisambiguationEdgeConnected([makeQuery(id+"F17.boolean.opBoolean","COPY",FACE,{"disambiguationData":[TD([makeQuery(id+"F14.opExtrude","CAP_FACE",FACE,{"disambiguationData":[OSD([subQ4,subQ3,subQ2,subQ1,subQ0])],"isStart":true})])],"derivedFrom":makeQuery(id+"F17.opExtrude","SWEPT_FACE",FACE,{"disambiguationData":[OSD([subQ5])]})}),makeQuery(id+"F18.opExtrude","SWEPT_FACE",FACE,{"disambiguationData":[OSD([sQuery(id+"F11.wireOp",EDGE,"E21"),subQ6])]}),makeQuery(id+"F18.opExtrude","SWEPT_FACE",FACE,{"disambiguationData":[OSD([subQ5])]})])],"derivedFrom":makeQuery(id+"F18.opExtrude","SWEPT_EDGE",EDGE,{"disambiguationData":[OSD([subQ6,subQ5])]})});}
            var Q49;
            {var subQ0=sQuery(id+"F8.wireOp",EDGE,"E7.right");var subQ1=sQuery(id+"F8.wireOp",EDGE,"E7.left");var subQ2=sQuery(id+"F8.wireOp",EDGE,"E7.top");var subQ3=sQuery(id+"F8.wireOp",EDGE,"E7.bottom");var subQ4=sQuery(id+"F8.wireOp",EDGE,"E6");var subQ5=sQuery(id+"F11.wireOp",EDGE,"E17");var subQ6=sQuery(id+"F11.wireOp",EDGE,"E23");Q49=makeQuery(id+"F17.boolean.opBoolean","COPY",EDGE,{"disambiguationData":[TD([makeQuery(id+"F14.opExtrude","CAP_FACE",FACE,{"disambiguationData":[OSD([subQ4,subQ3,subQ2,subQ1,subQ0])],"isStart":true})])],"derivedFrom":makeQuery(id+"F17.opExtrude","SWEPT_EDGE",EDGE,{"disambiguationData":[OSD([subQ5,subQ6])]})});}
            var Q50;
            {var subQ0=sQuery(id+"F11.wireOp",EDGE,"E17");var subQ1=sQuery(id+"F11.wireOp",EDGE,"E23");Q50=makeQuery(id+"F17.boolean.opBoolean","COPY",EDGE,{"disambiguationData":[TD([makeQuery(id+"F17.opExtrude","CAP_FACE",FACE,{"disambiguationData":[OSD([subQ0,subQ1,sQuery(id+"F11.wireOp",EDGE,"E39")])],"isStart":false})])],"derivedFrom":makeQuery(id+"F17.opExtrude","SWEPT_EDGE",EDGE,{"disambiguationData":[OSD([subQ0,subQ1])]})});}
            var Q51;
            {var subQ0=sQuery(id+"F11.wireOp",EDGE,"E17");var subQ1=sQuery(id+"F11.wireOp",EDGE,"E39");var subQ2=sQuery(id+"F11.wireOp",EDGE,"E23");var subQ3=sQuery(id+"F11.wireOp",EDGE,"E22");Q51=makeQuery(id+"F18.boolean.opBoolean","COPY",EDGE,{"disambiguationData":[topologyDisambiguationEdgeConnected([makeQuery(id+"F17.boolean.opBoolean","COPY",FACE,{"disambiguationData":[TD([makeQuery(id+"F17.opExtrude","CAP_FACE",FACE,{"disambiguationData":[OSD([subQ0,subQ2,subQ1])],"isStart":false})])],"derivedFrom":makeQuery(id+"F17.opExtrude","SWEPT_FACE",FACE,{"disambiguationData":[OSD([subQ2])]})}),makeQuery(id+"F18.opExtrude","SWEPT_FACE",FACE,{"disambiguationData":[OSD([sQuery(id+"F11.wireOp",EDGE,"E21"),subQ3])]}),makeQuery(id+"F18.opExtrude","SWEPT_FACE",FACE,{"disambiguationData":[OSD([subQ2])]})])],"derivedFrom":makeQuery(id+"F18.opExtrude","SWEPT_EDGE",EDGE,{"disambiguationData":[OSD([subQ3,subQ2])]})});}
            var Q52;
            {var subQ0=sQuery(id+"F11.wireOp",EDGE,"E18");var subQ1=sQuery(id+"F11.wireOp",EDGE,"E38");var subQ2=sQuery(id+"F11.wireOp",EDGE,"E19");var subQ3=sQuery(id+"F11.wireOp",EDGE,"E21");Q52=makeQuery(id+"F18.boolean.opBoolean","COPY",EDGE,{"disambiguationData":[topologyDisambiguationEdgeConnected([makeQuery(id+"F17.boolean.opBoolean","COPY",FACE,{"disambiguationData":[TD([makeQuery(id+"F17.opExtrude","CAP_FACE",FACE,{"disambiguationData":[OSD([subQ0,subQ2,subQ1])],"isStart":false})])],"derivedFrom":makeQuery(id+"F17.opExtrude","SWEPT_FACE",FACE,{"disambiguationData":[OSD([subQ2])]})}),makeQuery(id+"F18.opExtrude","SWEPT_FACE",FACE,{"disambiguationData":[OSD([subQ2])]}),makeQuery(id+"F18.opExtrude","SWEPT_FACE",FACE,{"disambiguationData":[OSD([subQ3,sQuery(id+"F11.wireOp",EDGE,"E22")])]})])],"derivedFrom":makeQuery(id+"F18.opExtrude","SWEPT_EDGE",EDGE,{"disambiguationData":[OSD([subQ2,subQ3])]})});}
            var Q53;
            {var subQ0=sQuery(id+"F11.wireOp",EDGE,"E18");var subQ1=sQuery(id+"F11.wireOp",EDGE,"E19");Q53=makeQuery(id+"F17.boolean.opBoolean","COPY",EDGE,{"disambiguationData":[TD([makeQuery(id+"F17.opExtrude","CAP_FACE",FACE,{"disambiguationData":[OSD([subQ0,subQ1,sQuery(id+"F11.wireOp",EDGE,"E38")])],"isStart":false})])],"derivedFrom":makeQuery(id+"F17.opExtrude","SWEPT_EDGE",EDGE,{"disambiguationData":[OSD([subQ0,subQ1])]})});}
            var Q54;
            Q54=makeQuery(id+"F17.boolean.opBoolean","COPY",EDGE,{"derivedFrom":makeQuery(id+"F17.opExtrude","CAP_EDGE",EDGE,{"disambiguationData":[OSD([sQuery(id+"F11.wireOp",EDGE,"E19")])],"isStart":false})});
            var Q55;
            Q55=makeQuery(id+"F17.boolean.opBoolean","COPY",EDGE,{"derivedFrom":makeQuery(id+"F17.opExtrude","CAP_EDGE",EDGE,{"disambiguationData":[OSD([sQuery(id+"F11.wireOp",EDGE,"E18")])],"isStart":false})});
            var Q56;
            Q56=makeQuery(id+"F17.boolean.opBoolean","COPY",EDGE,{"derivedFrom":makeQuery(id+"F17.opExtrude","CAP_EDGE",EDGE,{"disambiguationData":[OSD([sQuery(id+"F11.wireOp",EDGE,"E23")])],"isStart":false})});
            var Q57;
            Q57=makeQuery(id+"F17.boolean.opBoolean","COPY",EDGE,{"derivedFrom":makeQuery(id+"F17.opExtrude","CAP_EDGE",EDGE,{"disambiguationData":[OSD([sQuery(id+"F11.wireOp",EDGE,"E17")])],"isStart":false})});
            var Q58;
            {var subQ0=sQuery(id+"F11.wireOp",EDGE,"E18");var subQ1=sQuery(id+"F11.wireOp",EDGE,"E38");var subQ2=sQuery(id+"F11.wireOp",EDGE,"E19");Q58=makeQuery(id+"F18.boolean.opBoolean","COPY",EDGE,{"disambiguationData":[topologyDisambiguationEdgeConnected([makeQuery(id+"F17.boolean.opBoolean","COPY",FACE,{"disambiguationData":[TD([makeQuery(id+"F17.opExtrude","CAP_FACE",FACE,{"disambiguationData":[OSD([subQ0,subQ2,subQ1])],"isStart":false})])],"derivedFrom":makeQuery(id+"F17.opExtrude","SWEPT_FACE",FACE,{"disambiguationData":[OSD([subQ2])]})}),makeQuery(id+"F18.opExtrude","SWEPT_FACE",FACE,{"disambiguationData":[OSD([subQ2])]}),makeQuery(id+"F18.opExtrude","SWEPT_FACE",FACE,{"disambiguationData":[OSD([subQ1])]})])],"derivedFrom":makeQuery(id+"F18.opExtrude","SWEPT_EDGE",EDGE,{"disambiguationData":[OSD([subQ2,subQ1])]})});}
            var Q59;
            {var subQ1=sQuery(id+"F11.wireOp",EDGE,"E39");var subQ2=sQuery(id+"F11.wireOp",EDGE,"E23");var subQ3=sQuery(id+"F11.wireOp",EDGE,"E17");var subQ4=sQuery(id+"F11.wireOp",EDGE,"E38");var subQ5=sQuery(id+"F11.wireOp",EDGE,"E19");var subQ6=sQuery(id+"F11.wireOp",EDGE,"E18");Q59=makeQuery(id+"F18.boolean.opBoolean","COPY",EDGE,{"disambiguationData":[topologyDisambiguationEdgeConnected([makeQuery(id+"F17.boolean.opBoolean","COPY",FACE,{"disambiguationData":[TD([makeQuery(id+"F17.opExtrude","CAP_FACE",FACE,{"disambiguationData":[OSD([subQ3,subQ2,subQ1])],"isStart":false})])],"derivedFrom":makeQuery(id+"F17.opExtrude","SWEPT_FACE",FACE,{"disambiguationData":[OSD([subQ3])]})}),makeQuery(id+"F17.boolean.opBoolean","COPY",FACE,{"disambiguationData":[TD([makeQuery(id+"F17.opExtrude","CAP_FACE",FACE,{"disambiguationData":[OSD([subQ6,subQ5,subQ4])],"isStart":false})])],"derivedFrom":makeQuery(id+"F17.opExtrude","SWEPT_FACE",FACE,{"disambiguationData":[OSD([subQ6])]})}),makeQuery(id+"F18.opExtrude","SWEPT_FACE",FACE,{"disambiguationData":[OSD([subQ3,subQ6])]}),makeQuery(id+"F18.opExtrude","SWEPT_FACE",FACE,{"disambiguationData":[OSD([subQ4])]})])],"derivedFrom":makeQuery(id+"F18.opExtrude","SWEPT_EDGE",EDGE,{"disambiguationData":[OSD([subQ6,subQ4])]})});}
            var Q60;
            {var subQ1=sQuery(id+"F11.wireOp",EDGE,"E39");var subQ2=sQuery(id+"F11.wireOp",EDGE,"E23");var subQ3=sQuery(id+"F11.wireOp",EDGE,"E17");var subQ4=sQuery(id+"F11.wireOp",EDGE,"E38");var subQ5=sQuery(id+"F11.wireOp",EDGE,"E19");var subQ6=sQuery(id+"F11.wireOp",EDGE,"E18");Q60=makeQuery(id+"F18.boolean.opBoolean","COPY",EDGE,{"disambiguationData":[topologyDisambiguationEdgeConnected([makeQuery(id+"F17.boolean.opBoolean","COPY",FACE,{"disambiguationData":[TD([makeQuery(id+"F17.opExtrude","CAP_FACE",FACE,{"disambiguationData":[OSD([subQ3,subQ2,subQ1])],"isStart":false})])],"derivedFrom":makeQuery(id+"F17.opExtrude","SWEPT_FACE",FACE,{"disambiguationData":[OSD([subQ3])]})}),makeQuery(id+"F17.boolean.opBoolean","COPY",FACE,{"disambiguationData":[TD([makeQuery(id+"F17.opExtrude","CAP_FACE",FACE,{"disambiguationData":[OSD([subQ6,subQ5,subQ4])],"isStart":false})])],"derivedFrom":makeQuery(id+"F17.opExtrude","SWEPT_FACE",FACE,{"disambiguationData":[OSD([subQ6])]})}),makeQuery(id+"F18.opExtrude","SWEPT_FACE",FACE,{"disambiguationData":[OSD([subQ3,subQ6])]}),makeQuery(id+"F18.opExtrude","SWEPT_FACE",FACE,{"disambiguationData":[OSD([subQ1])]})])],"derivedFrom":makeQuery(id+"F18.opExtrude","SWEPT_EDGE",EDGE,{"disambiguationData":[OSD([subQ3,subQ1])]})});}
            var Q61;
            {var subQ0=sQuery(id+"F11.wireOp",EDGE,"E17");var subQ1=sQuery(id+"F11.wireOp",EDGE,"E39");var subQ2=sQuery(id+"F11.wireOp",EDGE,"E23");Q61=makeQuery(id+"F18.boolean.opBoolean","COPY",EDGE,{"disambiguationData":[topologyDisambiguationEdgeConnected([makeQuery(id+"F17.boolean.opBoolean","COPY",FACE,{"disambiguationData":[TD([makeQuery(id+"F17.opExtrude","CAP_FACE",FACE,{"disambiguationData":[OSD([subQ0,subQ2,subQ1])],"isStart":false})])],"derivedFrom":makeQuery(id+"F17.opExtrude","SWEPT_FACE",FACE,{"disambiguationData":[OSD([subQ2])]})}),makeQuery(id+"F18.opExtrude","SWEPT_FACE",FACE,{"disambiguationData":[OSD([subQ2])]}),makeQuery(id+"F18.opExtrude","SWEPT_FACE",FACE,{"disambiguationData":[OSD([subQ1])]})])],"derivedFrom":makeQuery(id+"F18.opExtrude","SWEPT_EDGE",EDGE,{"disambiguationData":[OSD([subQ2,subQ1])]})});}
            var Q62;
            {var subQ0=sQuery(id+"F11.wireOp",EDGE,"E18");var subQ1=sQuery(id+"F11.wireOp",EDGE,"E38");Q62=makeQuery(id+"F18.boolean.opBoolean","COPY",EDGE,{"disambiguationData":[topologyDisambiguationEdgeConnected([makeQuery(id+"F18.opExtrude","SWEPT_FACE",FACE,{"disambiguationData":[OSD([sQuery(id+"F11.wireOp",EDGE,"E17"),subQ0])]}),makeQuery(id+"F18.opExtrude","SWEPT_FACE",FACE,{"disambiguationData":[OSD([subQ1])]})])],"derivedFrom":makeQuery(id+"F18.opExtrude","SWEPT_EDGE",EDGE,{"disambiguationData":[OSD([subQ0,subQ1])]})});}
            var Q63;
            {var subQ0=sQuery(id+"F11.wireOp",EDGE,"E19");var subQ1=sQuery(id+"F11.wireOp",EDGE,"E38");Q63=makeQuery(id+"F18.boolean.opBoolean","COPY",EDGE,{"disambiguationData":[topologyDisambiguationEdgeConnected([makeQuery(id+"F18.opExtrude","SWEPT_FACE",FACE,{"disambiguationData":[OSD([subQ0])]}),makeQuery(id+"F18.opExtrude","SWEPT_FACE",FACE,{"disambiguationData":[OSD([subQ1])]})])],"derivedFrom":makeQuery(id+"F18.opExtrude","SWEPT_EDGE",EDGE,{"disambiguationData":[OSD([subQ0,subQ1])]})});}
            var Q64;
            {var subQ0=sQuery(id+"F11.wireOp",EDGE,"E17");var subQ1=sQuery(id+"F11.wireOp",EDGE,"E39");Q64=makeQuery(id+"F18.boolean.opBoolean","COPY",EDGE,{"disambiguationData":[topologyDisambiguationEdgeConnected([makeQuery(id+"F18.opExtrude","SWEPT_FACE",FACE,{"disambiguationData":[OSD([subQ0,sQuery(id+"F11.wireOp",EDGE,"E18")])]}),makeQuery(id+"F18.opExtrude","SWEPT_FACE",FACE,{"disambiguationData":[OSD([subQ1])]})])],"derivedFrom":makeQuery(id+"F18.opExtrude","SWEPT_EDGE",EDGE,{"disambiguationData":[OSD([subQ0,subQ1])]})});}
            var Q65;
            {var subQ0=sQuery(id+"F11.wireOp",EDGE,"E23");var subQ1=sQuery(id+"F11.wireOp",EDGE,"E39");Q65=makeQuery(id+"F18.boolean.opBoolean","COPY",EDGE,{"disambiguationData":[topologyDisambiguationEdgeConnected([makeQuery(id+"F18.opExtrude","SWEPT_FACE",FACE,{"disambiguationData":[OSD([subQ0])]}),makeQuery(id+"F18.opExtrude","SWEPT_FACE",FACE,{"disambiguationData":[OSD([subQ1])]})])],"derivedFrom":makeQuery(id+"F18.opExtrude","SWEPT_EDGE",EDGE,{"disambiguationData":[OSD([subQ0,subQ1])]})});}
            var Q66;
            {var subQ0=sQuery(id+"F11.wireOp",EDGE,"E22");var subQ1=sQuery(id+"F11.wireOp",EDGE,"E23");Q66=makeQuery(id+"F18.boolean.opBoolean","COPY",EDGE,{"disambiguationData":[topologyDisambiguationEdgeConnected([makeQuery(id+"F18.opExtrude","SWEPT_FACE",FACE,{"disambiguationData":[OSD([sQuery(id+"F11.wireOp",EDGE,"E21"),subQ0])]}),makeQuery(id+"F18.opExtrude","SWEPT_FACE",FACE,{"disambiguationData":[OSD([subQ1])]})])],"derivedFrom":makeQuery(id+"F18.opExtrude","SWEPT_EDGE",EDGE,{"disambiguationData":[OSD([subQ0,subQ1])]})});}
            var Q67;
            {var subQ0=sQuery(id+"F11.wireOp",EDGE,"E19");var subQ1=sQuery(id+"F11.wireOp",EDGE,"E21");Q67=makeQuery(id+"F18.boolean.opBoolean","COPY",EDGE,{"disambiguationData":[topologyDisambiguationEdgeConnected([makeQuery(id+"F18.opExtrude","SWEPT_FACE",FACE,{"disambiguationData":[OSD([subQ0])]}),makeQuery(id+"F18.opExtrude","SWEPT_FACE",FACE,{"disambiguationData":[OSD([subQ1,sQuery(id+"F11.wireOp",EDGE,"E22")])]})])],"derivedFrom":makeQuery(id+"F18.opExtrude","SWEPT_EDGE",EDGE,{"disambiguationData":[OSD([subQ0,subQ1])]})});}
            fillet(context, id + "F40", {"entities" : qUnion([Q0, Q1, Q2, Q3, Q4, Q5, Q6, Q7, Q8, Q9, Q10, Q11, Q12, Q13, Q14, Q15, Q16, Q17, Q18, Q19, Q20, Q21, Q22, Q23, Q24, Q25, Q26, Q27, Q28, Q29, Q30, Q31, Q32, Q33, Q34, Q35, Q36, Q37, Q38, Q39, Q40, Q41, Q42, Q43, Q44, Q45, Q46, Q47, Q48, Q49, Q50, Q51, Q52, Q53, Q54, Q55, Q56, Q57, Q58, Q59, Q60, Q61, Q62, Q63, Q64, Q65, Q66, Q67]), "radius" : 3 * mm, "tangentPropagation" : true, "allowEdgeOverflow" : false});
        }
    });
